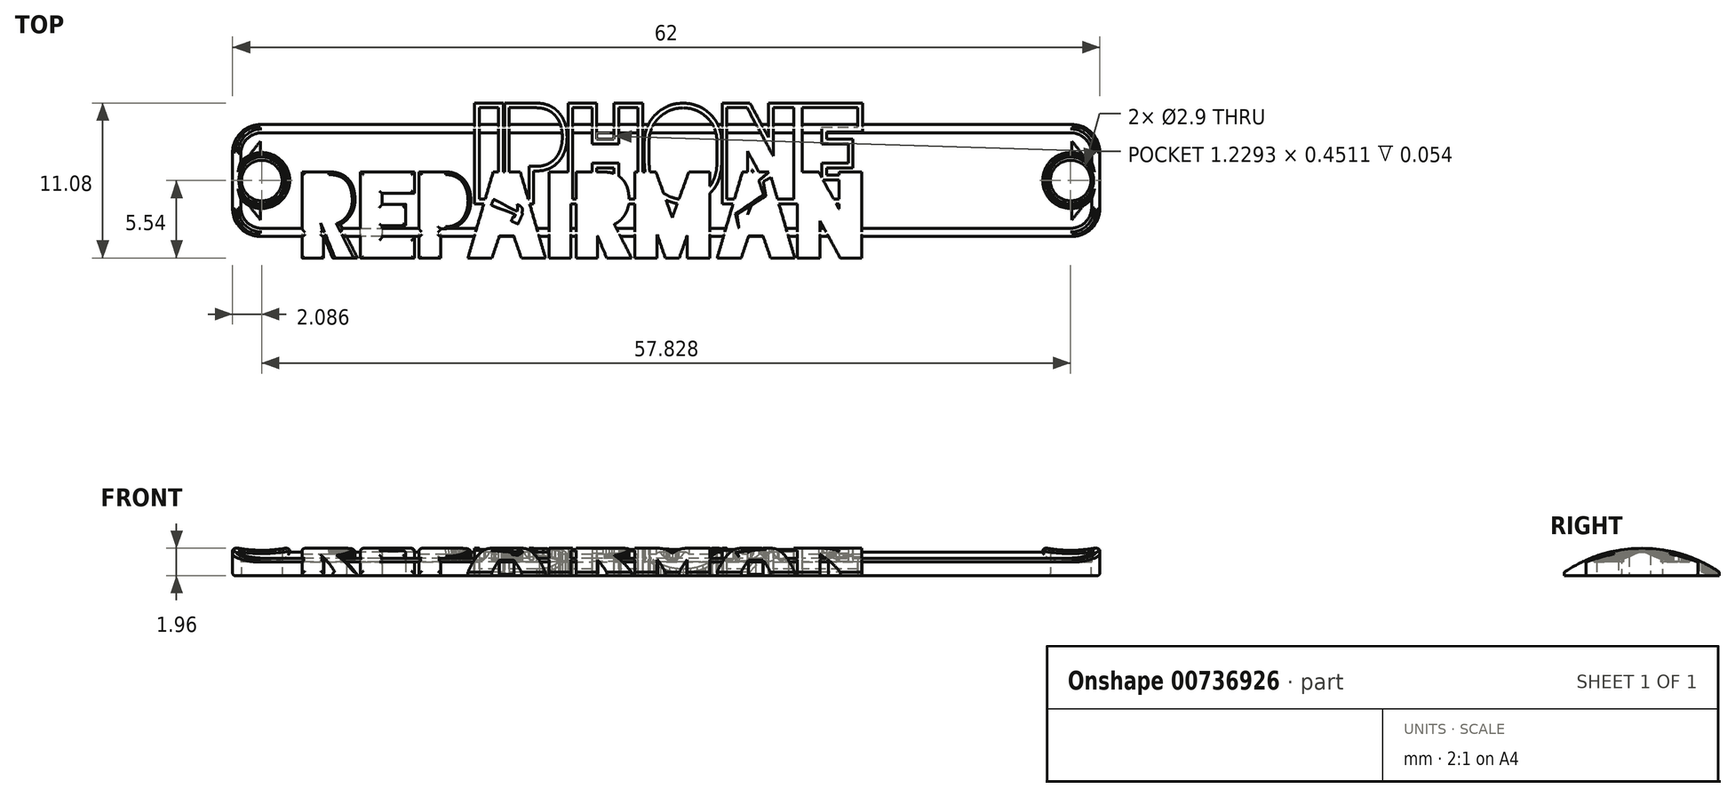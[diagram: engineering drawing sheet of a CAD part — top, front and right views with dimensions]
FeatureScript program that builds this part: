
annotation { "Feature Type Name" : "Feature", "Feature Type Description" : "" }
export const myFeature = defineFeature(function(context is Context, id is Id, definition is map)
    precondition{}
    {
        {
            var Q0;
            Q0=qCreatedBy(makeId("Top.planeOp"),FACE);
            var sketch = newSketch(context, id + "F0", { "sketchPlane" : qUnion([Q0])});
            skLineSegment(sketch, "E0", {"start": v(19.57, 7.6) * mm, "end": v(19.84, 6.63) * mm});
            skLineSegment(sketch, "E1", {"start": v(19.84, 6.63) * mm, "end": v(19.94, 5.63) * mm});
            skLineSegment(sketch, "E2", {"start": v(19.94, 5.63) * mm, "end": v(19.94, 5.62) * mm});
            skLineSegment(sketch, "E3", {"start": v(19.94, 5.62) * mm, "end": v(19.94, 2.5) * mm});
            skLineSegment(sketch, "E4", {"start": v(19.94, 2.5) * mm, "end": v(19.86, 1.44) * mm});
            skLineSegment(sketch, "E5", {"start": v(19.86, 1.44) * mm, "end": v(19.6, 0.37) * mm});
            skLineSegment(sketch, "E6", {"start": v(19.6, 0.37) * mm, "end": v(19.51, 0.1) * mm});
            skLineSegment(sketch, "E7", {"start": v(19.51, 0.1) * mm, "end": v(19.41, -0.17) * mm});
            skLineSegment(sketch, "E8", {"start": v(19.41, -0.17) * mm, "end": v(19.3, -0.42) * mm});
            skLineSegment(sketch, "E9", {"start": v(19.3, -0.42) * mm, "end": v(19.16, -0.67) * mm});
            skLineSegment(sketch, "E10", {"start": v(19.16, -0.67) * mm, "end": v(19.02, -0.9) * mm});
            skLineSegment(sketch, "E11", {"start": v(19.02, -0.9) * mm, "end": v(18.86, -1.14) * mm});
            skLineSegment(sketch, "E12", {"start": v(18.86, -1.14) * mm, "end": v(18.68, -1.36) * mm});
            skLineSegment(sketch, "E13", {"start": v(18.68, -1.36) * mm, "end": v(18.5, -1.57) * mm});
            skLineSegment(sketch, "E14", {"start": v(18.5, -1.57) * mm, "end": v(18.5, -1.57) * mm});
            skLineSegment(sketch, "E15", {"start": v(18.5, -1.57) * mm, "end": v(18.25, -1.82) * mm});
            skLineSegment(sketch, "E16", {"start": v(18.25, -1.82) * mm, "end": v(18.25, -11.08) * mm});
            skLineSegment(sketch, "E17", {"start": v(18.25, -11.08) * mm, "end": v(15, -11.08) * mm});
            skLineSegment(sketch, "E18", {"start": v(15, -11.08) * mm, "end": v(15, -7.86) * mm});
            skLineSegment(sketch, "E19", {"start": v(15, -7.86) * mm, "end": v(13.87, -11.08) * mm});
            skLineSegment(sketch, "E20", {"start": v(13.87, -11.08) * mm, "end": v(11.88, -11.08) * mm});
            skLineSegment(sketch, "E21", {"start": v(11.88, -11.08) * mm, "end": v(10.7, -7.7) * mm});
            skLineSegment(sketch, "E22", {"start": v(10.7, -7.7) * mm, "end": v(10.7, -11.08) * mm});
            skLineSegment(sketch, "E23", {"start": v(10.7, -11.08) * mm, "end": v(7.48, -11.08) * mm});
            skLineSegment(sketch, "E24", {"start": v(7.48, -11.08) * mm, "end": v(7.48, -3.35) * mm});
            skLineSegment(sketch, "E25", {"start": v(7.48, -3.35) * mm, "end": v(6.65, -3.35) * mm});
            skLineSegment(sketch, "E26", {"start": v(6.65, -3.35) * mm, "end": v(6.46, -4.12) * mm});
            skLineSegment(sketch, "E27", {"start": v(6.46, -4.12) * mm, "end": v(6.35, -4.4) * mm});
            skLineSegment(sketch, "E28", {"start": v(6.35, -4.4) * mm, "end": v(6.21, -4.68) * mm});
            skLineSegment(sketch, "E29", {"start": v(6.21, -4.68) * mm, "end": v(6.07, -4.92) * mm});
            skLineSegment(sketch, "E30", {"start": v(6.07, -4.92) * mm, "end": v(5.91, -5.15) * mm});
            skLineSegment(sketch, "E31", {"start": v(5.91, -5.15) * mm, "end": v(5.75, -5.36) * mm});
            skLineSegment(sketch, "E32", {"start": v(5.75, -5.36) * mm, "end": v(5.58, -5.54) * mm});
            skLineSegment(sketch, "E33", {"start": v(5.58, -5.54) * mm, "end": v(5.4, -5.71) * mm});
            skLineSegment(sketch, "E34", {"start": v(5.4, -5.71) * mm, "end": v(5.22, -5.86) * mm});
            skLineSegment(sketch, "E35", {"start": v(5.22, -5.86) * mm, "end": v(5.05, -6) * mm});
            skLineSegment(sketch, "E36", {"start": v(5.05, -6) * mm, "end": v(4.88, -6.1) * mm});
            skLineSegment(sketch, "E37", {"start": v(4.88, -6.1) * mm, "end": v(4.73, -6.19) * mm});
            skLineSegment(sketch, "E38", {"start": v(4.73, -6.19) * mm, "end": v(4.58, -6.25) * mm});
            skLineSegment(sketch, "E39", {"start": v(4.58, -6.25) * mm, "end": v(5.82, -8.67) * mm});
            skLineSegment(sketch, "E40", {"start": v(5.82, -8.67) * mm, "end": v(7.04, -11.08) * mm});
            skLineSegment(sketch, "E41", {"start": v(7.04, -11.08) * mm, "end": v(3.5, -11.08) * mm});
            skLineSegment(sketch, "E42", {"start": v(3.5, -11.08) * mm, "end": v(2.18, -7.94) * mm});
            skLineSegment(sketch, "E43", {"start": v(2.18, -7.94) * mm, "end": v(2.18, -11.08) * mm});
            skLineSegment(sketch, "E44", {"start": v(2.18, -11.08) * mm, "end": v(-0.9, -11.08) * mm});
            skLineSegment(sketch, "E45", {"start": v(-0.9, -11.08) * mm, "end": v(-0.9, -3.35) * mm});
            skLineSegment(sketch, "E46", {"start": v(-0.9, -3.35) * mm, "end": v(-1.66, -3.35) * mm});
            skLineSegment(sketch, "E47", {"start": v(-1.66, -3.35) * mm, "end": v(-1.66, -11.08) * mm});
            skLineSegment(sketch, "E48", {"start": v(-1.66, -11.08) * mm, "end": v(-4.74, -11.08) * mm});
            skLineSegment(sketch, "E49", {"start": v(-4.74, -11.08) * mm, "end": v(-4.74, 1.23) * mm});
            skLineSegment(sketch, "E50", {"start": v(-4.74, 1.23) * mm, "end": v(-2.03, 1.23) * mm});
            skLineSegment(sketch, "E51", {"start": v(-2.03, 1.23) * mm, "end": v(-2.03, 11.08) * mm});
            skLineSegment(sketch, "E52", {"start": v(-2.03, 11.08) * mm, "end": v(2.08, 11.08) * mm});
            skLineSegment(sketch, "E53", {"start": v(2.08, 11.08) * mm, "end": v(2.08, 5.93) * mm});
            skLineSegment(sketch, "E54", {"start": v(2.08, 5.93) * mm, "end": v(4.54, 5.93) * mm});
            skLineSegment(sketch, "E55", {"start": v(4.54, 5.93) * mm, "end": v(4.54, 11.08) * mm});
            skLineSegment(sketch, "E56", {"start": v(4.54, 11.08) * mm, "end": v(4.88, 11.08) * mm});
            skLineSegment(sketch, "E57", {"start": v(4.88, 11.08) * mm, "end": v(8.65, 11.08) * mm});
            skLineSegment(sketch, "E58", {"start": v(8.65, 11.08) * mm, "end": v(8.65, 1.23) * mm});
            skLineSegment(sketch, "E59", {"start": v(8.65, 1.23) * mm, "end": v(8.98, 1.23) * mm});
            skLineSegment(sketch, "E60", {"start": v(8.98, 1.23) * mm, "end": v(8.96, 1.38) * mm});
            skLineSegment(sketch, "E61", {"start": v(8.96, 1.38) * mm, "end": v(8.87, 2.5) * mm});
            skLineSegment(sketch, "E62", {"start": v(8.87, 2.5) * mm, "end": v(8.87, 2.5) * mm});
            skLineSegment(sketch, "E63", {"start": v(8.87, 2.5) * mm, "end": v(8.87, 5.62) * mm});
            skLineSegment(sketch, "E64", {"start": v(8.87, 5.62) * mm, "end": v(8.96, 6.6) * mm});
            skLineSegment(sketch, "E65", {"start": v(8.96, 6.6) * mm, "end": v(9.24, 7.58) * mm});
            skLineSegment(sketch, "E66", {"start": v(9.24, 7.58) * mm, "end": v(9.7, 8.5) * mm});
            skLineSegment(sketch, "E67", {"start": v(9.7, 8.5) * mm, "end": v(10.32, 9.3) * mm});
            skLineSegment(sketch, "E68", {"start": v(10.32, 9.3) * mm, "end": v(10.32, 9.3) * mm});
            skLineSegment(sketch, "E69", {"start": v(10.32, 9.3) * mm, "end": v(11.2, 10.06) * mm});
            skLineSegment(sketch, "E70", {"start": v(11.2, 10.06) * mm, "end": v(12.2, 10.62) * mm});
            skLineSegment(sketch, "E71", {"start": v(12.2, 10.62) * mm, "end": v(12.2, 10.62) * mm});
            skLineSegment(sketch, "E72", {"start": v(12.2, 10.62) * mm, "end": v(12.46, 10.73) * mm});
            skLineSegment(sketch, "E73", {"start": v(12.46, 10.73) * mm, "end": v(12.72, 10.82) * mm});
            skLineSegment(sketch, "E74", {"start": v(12.72, 10.82) * mm, "end": v(13, 10.9) * mm});
            skLineSegment(sketch, "E75", {"start": v(13, 10.9) * mm, "end": v(13.27, 10.97) * mm});
            skLineSegment(sketch, "E76", {"start": v(13.27, 10.97) * mm, "end": v(14.42, 11.08) * mm});
            skLineSegment(sketch, "E77", {"start": v(14.42, 11.08) * mm, "end": v(15.56, 10.96) * mm});
            skLineSegment(sketch, "E78", {"start": v(15.56, 10.96) * mm, "end": v(16.64, 10.62) * mm});
            skLineSegment(sketch, "E79", {"start": v(16.64, 10.62) * mm, "end": v(16.9, 10.5) * mm});
            skLineSegment(sketch, "E80", {"start": v(16.9, 10.5) * mm, "end": v(17.15, 10.37) * mm});
            skLineSegment(sketch, "E81", {"start": v(17.15, 10.37) * mm, "end": v(17.4, 10.22) * mm});
            skLineSegment(sketch, "E82", {"start": v(17.4, 10.22) * mm, "end": v(17.63, 10.06) * mm});
            skLineSegment(sketch, "E83", {"start": v(17.63, 10.06) * mm, "end": v(18.5, 9.3) * mm});
            skLineSegment(sketch, "E84", {"start": v(18.5, 9.3) * mm, "end": v(19.12, 8.51) * mm});
            skLineSegment(sketch, "E85", {"start": v(19.12, 8.51) * mm, "end": v(19.57, 7.6) * mm});
            skLineSegment(sketch, "E86", {"start": v(7.48, -2.67) * mm, "end": v(7.48, 1.23) * mm});
            skLineSegment(sketch, "E87", {"start": v(7.48, 1.23) * mm, "end": v(7.97, 1.23) * mm});
            skLineSegment(sketch, "E88", {"start": v(7.97, 1.23) * mm, "end": v(7.97, 10.4) * mm});
            skLineSegment(sketch, "E89", {"start": v(7.97, 10.4) * mm, "end": v(5.22, 10.4) * mm});
            skLineSegment(sketch, "E90", {"start": v(5.22, 10.4) * mm, "end": v(5.22, 5.25) * mm});
            skLineSegment(sketch, "E91", {"start": v(5.22, 5.25) * mm, "end": v(1.4, 5.25) * mm});
            skLineSegment(sketch, "E92", {"start": v(1.4, 5.25) * mm, "end": v(1.4, 10.4) * mm});
            skLineSegment(sketch, "E93", {"start": v(1.4, 10.4) * mm, "end": v(-1.35, 10.4) * mm});
            skLineSegment(sketch, "E94", {"start": v(-1.35, 10.4) * mm, "end": v(-1.35, -2.67) * mm});
            skLineSegment(sketch, "E95", {"start": v(-1.35, -2.67) * mm, "end": v(-0.9, -2.67) * mm});
            skLineSegment(sketch, "E96", {"start": v(-0.9, -2.67) * mm, "end": v(-0.9, 1.23) * mm});
            skLineSegment(sketch, "E97", {"start": v(-0.9, 1.23) * mm, "end": v(1.4, 1.23) * mm});
            skLineSegment(sketch, "E98", {"start": v(1.4, 1.23) * mm, "end": v(1.4, 2.48) * mm});
            skLineSegment(sketch, "E99", {"start": v(1.4, 2.48) * mm, "end": v(5.22, 2.48) * mm});
            skLineSegment(sketch, "E100", {"start": v(5.22, 2.48) * mm, "end": v(5.22, 0.64) * mm});
            skLineSegment(sketch, "E101", {"start": v(5.22, 0.64) * mm, "end": v(5.4, 0.5) * mm});
            skLineSegment(sketch, "E102", {"start": v(5.4, 0.5) * mm, "end": v(5.58, 0.35) * mm});
            skLineSegment(sketch, "E103", {"start": v(5.58, 0.35) * mm, "end": v(5.74, 0.2) * mm});
            skLineSegment(sketch, "E104", {"start": v(5.74, 0.2) * mm, "end": v(5.89, 0.02) * mm});
            skLineSegment(sketch, "E105", {"start": v(5.89, 0.02) * mm, "end": v(6.09, -0.26) * mm});
            skLineSegment(sketch, "E106", {"start": v(6.09, -0.26) * mm, "end": v(6.26, -0.57) * mm});
            skLineSegment(sketch, "E107", {"start": v(6.26, -0.57) * mm, "end": v(6.4, -0.9) * mm});
            skLineSegment(sketch, "E108", {"start": v(6.4, -0.9) * mm, "end": v(6.5, -1.26) * mm});
            skLineSegment(sketch, "E109", {"start": v(6.5, -1.26) * mm, "end": v(6.58, -1.6) * mm});
            skLineSegment(sketch, "E110", {"start": v(6.58, -1.6) * mm, "end": v(6.64, -1.95) * mm});
            skLineSegment(sketch, "E111", {"start": v(6.64, -1.95) * mm, "end": v(6.67, -2.3) * mm});
            skLineSegment(sketch, "E112", {"start": v(6.67, -2.3) * mm, "end": v(6.69, -2.67) * mm});
            skLineSegment(sketch, "E113", {"start": v(6.69, -2.67) * mm, "end": v(7.48, -2.67) * mm});
            skLineSegment(sketch, "E114", {"start": v(4.54, 0.99) * mm, "end": v(4.54, 1.8) * mm});
            skLineSegment(sketch, "E115", {"start": v(4.54, 1.8) * mm, "end": v(2.08, 1.8) * mm});
            skLineSegment(sketch, "E116", {"start": v(2.08, 1.8) * mm, "end": v(2.08, 1.23) * mm});
            skLineSegment(sketch, "E117", {"start": v(2.08, 1.23) * mm, "end": v(2.94, 1.23) * mm});
            skLineSegment(sketch, "E118", {"start": v(2.94, 1.23) * mm, "end": v(3.4, 1.21) * mm});
            skLineSegment(sketch, "E119", {"start": v(3.4, 1.21) * mm, "end": v(3.8, 1.17) * mm});
            skLineSegment(sketch, "E120", {"start": v(3.8, 1.17) * mm, "end": v(4.19, 1.1) * mm});
            skLineSegment(sketch, "E121", {"start": v(4.19, 1.1) * mm, "end": v(4.54, 0.99) * mm});
            skLineSegment(sketch, "E122", {"start": v(13.59, -3.3) * mm, "end": v(13.27, -3.25) * mm});
            skLineSegment(sketch, "E123", {"start": v(13.27, -3.25) * mm, "end": v(12.2, -2.9) * mm});
            skLineSegment(sketch, "E124", {"start": v(12.2, -2.9) * mm, "end": v(11.98, -2.8) * mm});
            skLineSegment(sketch, "E125", {"start": v(11.98, -2.8) * mm, "end": v(12.88, -5.3) * mm});
            skLineSegment(sketch, "E126", {"start": v(12.88, -5.3) * mm, "end": v(13.59, -3.3) * mm});
            skLineSegment(sketch, "E127", {"start": v(15.23, 1.23) * mm, "end": v(18.25, 1.23) * mm});
            skLineSegment(sketch, "E128", {"start": v(18.25, 1.23) * mm, "end": v(18.25, -0.82) * mm});
            skLineSegment(sketch, "E129", {"start": v(18.25, -0.82) * mm, "end": v(18.58, -0.33) * mm});
            skLineSegment(sketch, "E130", {"start": v(18.58, -0.33) * mm, "end": v(18.96, 0.56) * mm});
            skLineSegment(sketch, "E131", {"start": v(18.96, 0.56) * mm, "end": v(18.96, 0.57) * mm});
            skLineSegment(sketch, "E132", {"start": v(18.96, 0.57) * mm, "end": v(19.2, 1.54) * mm});
            skLineSegment(sketch, "E133", {"start": v(19.2, 1.54) * mm, "end": v(19.27, 2.5) * mm});
            skLineSegment(sketch, "E134", {"start": v(19.27, 2.5) * mm, "end": v(19.27, 5.62) * mm});
            skLineSegment(sketch, "E135", {"start": v(19.27, 5.62) * mm, "end": v(19.27, 5.62) * mm});
            skLineSegment(sketch, "E136", {"start": v(19.27, 5.62) * mm, "end": v(19.18, 6.51) * mm});
            skLineSegment(sketch, "E137", {"start": v(19.18, 6.51) * mm, "end": v(18.94, 7.36) * mm});
            skLineSegment(sketch, "E138", {"start": v(18.94, 7.36) * mm, "end": v(18.94, 7.37) * mm});
            skLineSegment(sketch, "E139", {"start": v(18.94, 7.37) * mm, "end": v(18.55, 8.15) * mm});
            skLineSegment(sketch, "E140", {"start": v(18.55, 8.15) * mm, "end": v(18.01, 8.84) * mm});
            skLineSegment(sketch, "E141", {"start": v(18.01, 8.84) * mm, "end": v(18, 8.84) * mm});
            skLineSegment(sketch, "E142", {"start": v(18, 8.84) * mm, "end": v(17.24, 9.51) * mm});
            skLineSegment(sketch, "E143", {"start": v(17.24, 9.51) * mm, "end": v(16.37, 10) * mm});
            skLineSegment(sketch, "E144", {"start": v(16.37, 10) * mm, "end": v(15.42, 10.3) * mm});
            skLineSegment(sketch, "E145", {"start": v(15.42, 10.3) * mm, "end": v(14.42, 10.4) * mm});
            skLineSegment(sketch, "E146", {"start": v(14.42, 10.4) * mm, "end": v(13.4, 10.3) * mm});
            skLineSegment(sketch, "E147", {"start": v(13.4, 10.3) * mm, "end": v(12.47, 10) * mm});
            skLineSegment(sketch, "E148", {"start": v(12.47, 10) * mm, "end": v(11.59, 9.5) * mm});
            skLineSegment(sketch, "E149", {"start": v(11.59, 9.5) * mm, "end": v(10.81, 8.84) * mm});
            skLineSegment(sketch, "E150", {"start": v(10.81, 8.84) * mm, "end": v(10.27, 8.14) * mm});
            skLineSegment(sketch, "E151", {"start": v(10.27, 8.14) * mm, "end": v(9.88, 7.34) * mm});
            skLineSegment(sketch, "E152", {"start": v(9.88, 7.34) * mm, "end": v(9.88, 7.34) * mm});
            skLineSegment(sketch, "E153", {"start": v(9.88, 7.34) * mm, "end": v(9.63, 6.47) * mm});
            skLineSegment(sketch, "E154", {"start": v(9.63, 6.47) * mm, "end": v(9.55, 5.62) * mm});
            skLineSegment(sketch, "E155", {"start": v(9.55, 5.62) * mm, "end": v(9.55, 2.5) * mm});
            skLineSegment(sketch, "E156", {"start": v(9.55, 2.5) * mm, "end": v(9.55, 2.5) * mm});
            skLineSegment(sketch, "E157", {"start": v(9.55, 2.5) * mm, "end": v(9.63, 1.48) * mm});
            skLineSegment(sketch, "E158", {"start": v(9.63, 1.48) * mm, "end": v(9.67, 1.23) * mm});
            skLineSegment(sketch, "E159", {"start": v(9.67, 1.23) * mm, "end": v(10.53, 1.23) * mm});
            skLineSegment(sketch, "E160", {"start": v(10.53, 1.23) * mm, "end": v(11.63, -1.82) * mm});
            skLineSegment(sketch, "E161", {"start": v(11.63, -1.82) * mm, "end": v(12.47, -2.29) * mm});
            skLineSegment(sketch, "E162", {"start": v(12.47, -2.29) * mm, "end": v(13.4, -2.59) * mm});
            skLineSegment(sketch, "E163", {"start": v(13.4, -2.59) * mm, "end": v(13.4, -2.59) * mm});
            skLineSegment(sketch, "E164", {"start": v(13.4, -2.59) * mm, "end": v(13.82, -2.65) * mm});
            skLineSegment(sketch, "E165", {"start": v(13.82, -2.65) * mm, "end": v(14.05, -2.03) * mm});
            skLineSegment(sketch, "E166", {"start": v(14.05, -2.03) * mm, "end": v(15.23, 1.23) * mm});
            skLineSegment(sketch, "E167", {"start": v(26.97, 11.08) * mm, "end": v(30.92, 11.08) * mm});
            skLineSegment(sketch, "E168", {"start": v(30.92, 11.08) * mm, "end": v(30.92, -3.35) * mm});
            skLineSegment(sketch, "E169", {"start": v(30.92, -3.35) * mm, "end": v(28.11, -3.35) * mm});
            skLineSegment(sketch, "E170", {"start": v(28.11, -3.35) * mm, "end": v(30.37, -11.08) * mm});
            skLineSegment(sketch, "E171", {"start": v(30.37, -11.08) * mm, "end": v(26.93, -11.08) * mm});
            skLineSegment(sketch, "E172", {"start": v(26.93, -11.08) * mm, "end": v(25.84, -7.94) * mm});
            skLineSegment(sketch, "E173", {"start": v(25.84, -7.94) * mm, "end": v(23.79, -7.94) * mm});
            skLineSegment(sketch, "E174", {"start": v(23.79, -7.94) * mm, "end": v(22.73, -11.08) * mm});
            skLineSegment(sketch, "E175", {"start": v(22.73, -11.08) * mm, "end": v(19.29, -11.08) * mm});
            skLineSegment(sketch, "E176", {"start": v(19.29, -11.08) * mm, "end": v(21.55, -3.35) * mm});
            skLineSegment(sketch, "E177", {"start": v(21.55, -3.35) * mm, "end": v(20, -3.35) * mm});
            skLineSegment(sketch, "E178", {"start": v(20, -3.35) * mm, "end": v(20, 11.08) * mm});
            skLineSegment(sketch, "E179", {"start": v(20, 11.08) * mm, "end": v(23.96, 11.08) * mm});
            skLineSegment(sketch, "E180", {"start": v(23.96, 11.08) * mm, "end": v(26.63, 6.17) * mm});
            skLineSegment(sketch, "E181", {"start": v(26.63, 6.17) * mm, "end": v(26.63, 11.08) * mm});
            skLineSegment(sketch, "E182", {"start": v(26.63, 11.08) * mm, "end": v(26.97, 11.08) * mm});
            skLineSegment(sketch, "E183", {"start": v(24.48, 1.23) * mm, "end": v(24.3, 1.57) * mm});
            skLineSegment(sketch, "E184", {"start": v(24.3, 1.57) * mm, "end": v(24.3, 1.23) * mm});
            skLineSegment(sketch, "E185", {"start": v(24.3, 1.23) * mm, "end": v(24.48, 1.23) * mm});
            skLineSegment(sketch, "E186", {"start": v(27, 0.44) * mm, "end": v(27.91, -2.67) * mm});
            skLineSegment(sketch, "E187", {"start": v(27.91, -2.67) * mm, "end": v(30.25, -2.67) * mm});
            skLineSegment(sketch, "E188", {"start": v(30.25, -2.67) * mm, "end": v(30.25, 10.4) * mm});
            skLineSegment(sketch, "E189", {"start": v(30.25, 10.4) * mm, "end": v(27.3, 10.4) * mm});
            skLineSegment(sketch, "E190", {"start": v(27.3, 10.4) * mm, "end": v(27.3, 3.5) * mm});
            skLineSegment(sketch, "E191", {"start": v(27.3, 3.5) * mm, "end": v(23.56, 10.4) * mm});
            skLineSegment(sketch, "E192", {"start": v(23.56, 10.4) * mm, "end": v(20.68, 10.4) * mm});
            skLineSegment(sketch, "E193", {"start": v(20.68, 10.4) * mm, "end": v(20.68, -2.67) * mm});
            skLineSegment(sketch, "E194", {"start": v(20.68, -2.67) * mm, "end": v(21.75, -2.67) * mm});
            skLineSegment(sketch, "E195", {"start": v(21.75, -2.67) * mm, "end": v(22.9, 1.23) * mm});
            skLineSegment(sketch, "E196", {"start": v(22.9, 1.23) * mm, "end": v(23.62, 1.23) * mm});
            skLineSegment(sketch, "E197", {"start": v(23.62, 1.23) * mm, "end": v(23.62, 4.22) * mm});
            skLineSegment(sketch, "E198", {"start": v(23.62, 4.22) * mm, "end": v(25.25, 1.23) * mm});
            skLineSegment(sketch, "E199", {"start": v(25.25, 1.23) * mm, "end": v(26.71, 1.23) * mm});
            skLineSegment(sketch, "E200", {"start": v(26.71, 1.23) * mm, "end": v(25.25, -0.02) * mm});
            skLineSegment(sketch, "E201", {"start": v(25.25, -0.02) * mm, "end": v(25.9, -2) * mm});
            skLineSegment(sketch, "E202", {"start": v(25.9, -2) * mm, "end": v(21.89, -4.75) * mm});
            skLineSegment(sketch, "E203", {"start": v(21.89, -4.75) * mm, "end": v(22.4, -6.86) * mm});
            skLineSegment(sketch, "E204", {"start": v(22.4, -6.86) * mm, "end": v(22.1, -4.84) * mm});
            skLineSegment(sketch, "E205", {"start": v(22.1, -4.84) * mm, "end": v(24.02, -3.63) * mm});
            skLineSegment(sketch, "E206", {"start": v(24.02, -3.63) * mm, "end": v(23.63, -4.9) * mm});
            skLineSegment(sketch, "E207", {"start": v(23.63, -4.9) * mm, "end": v(24.23, -3.5) * mm});
            skLineSegment(sketch, "E208", {"start": v(24.23, -3.5) * mm, "end": v(26.24, -2.23) * mm});
            skLineSegment(sketch, "E209", {"start": v(26.24, -2.23) * mm, "end": v(25.88, -0.14) * mm});
            skLineSegment(sketch, "E210", {"start": v(25.88, -0.14) * mm, "end": v(27, 0.44) * mm});
            skLineSegment(sketch, "E211", {"start": v(-33.37, -8.67) * mm, "end": v(-32.14, -11.08) * mm});
            skLineSegment(sketch, "E212", {"start": v(-32.14, -11.08) * mm, "end": v(-35.69, -11.08) * mm});
            skLineSegment(sketch, "E213", {"start": v(-35.69, -11.08) * mm, "end": v(-37, -7.94) * mm});
            skLineSegment(sketch, "E214", {"start": v(-37, -7.94) * mm, "end": v(-37, -11.08) * mm});
            skLineSegment(sketch, "E215", {"start": v(-37, -11.08) * mm, "end": v(-40.07, -11.08) * mm});
            skLineSegment(sketch, "E216", {"start": v(-40.07, -11.08) * mm, "end": v(-40.07, 1.23) * mm});
            skLineSegment(sketch, "E217", {"start": v(-40.07, 1.23) * mm, "end": v(-36.24, 1.23) * mm});
            skLineSegment(sketch, "E218", {"start": v(-36.24, 1.23) * mm, "end": v(-35.98, 1.22) * mm});
            skLineSegment(sketch, "E219", {"start": v(-35.98, 1.22) * mm, "end": v(-35.73, 1.2) * mm});
            skLineSegment(sketch, "E220", {"start": v(-35.73, 1.2) * mm, "end": v(-35.49, 1.18) * mm});
            skLineSegment(sketch, "E221", {"start": v(-35.49, 1.18) * mm, "end": v(-35.26, 1.15) * mm});
            skLineSegment(sketch, "E222", {"start": v(-35.26, 1.15) * mm, "end": v(-35.04, 1.1) * mm});
            skLineSegment(sketch, "E223", {"start": v(-35.04, 1.1) * mm, "end": v(-34.83, 1.05) * mm});
            skLineSegment(sketch, "E224", {"start": v(-34.83, 1.05) * mm, "end": v(-34.63, 0.98) * mm});
            skLineSegment(sketch, "E225", {"start": v(-34.63, 0.98) * mm, "end": v(-34.45, 0.9) * mm});
            skLineSegment(sketch, "E226", {"start": v(-34.45, 0.9) * mm, "end": v(-34.27, 0.82) * mm});
            skLineSegment(sketch, "E227", {"start": v(-34.27, 0.82) * mm, "end": v(-34.1, 0.73) * mm});
            skLineSegment(sketch, "E228", {"start": v(-34.1, 0.73) * mm, "end": v(-33.95, 0.63) * mm});
            skLineSegment(sketch, "E229", {"start": v(-33.95, 0.63) * mm, "end": v(-33.8, 0.52) * mm});
            skLineSegment(sketch, "E230", {"start": v(-33.8, 0.52) * mm, "end": v(-33.66, 0.4) * mm});
            skLineSegment(sketch, "E231", {"start": v(-33.66, 0.4) * mm, "end": v(-33.53, 0.28) * mm});
            skLineSegment(sketch, "E232", {"start": v(-33.53, 0.28) * mm, "end": v(-33.4, 0.16) * mm});
            skLineSegment(sketch, "E233", {"start": v(-33.4, 0.16) * mm, "end": v(-33.3, 0.02) * mm});
            skLineSegment(sketch, "E234", {"start": v(-33.3, 0.02) * mm, "end": v(-33.1, -0.26) * mm});
            skLineSegment(sketch, "E235", {"start": v(-33.1, -0.26) * mm, "end": v(-32.92, -0.57) * mm});
            skLineSegment(sketch, "E236", {"start": v(-32.92, -0.57) * mm, "end": v(-32.79, -0.9) * mm});
            skLineSegment(sketch, "E237", {"start": v(-32.79, -0.9) * mm, "end": v(-32.68, -1.26) * mm});
            skLineSegment(sketch, "E238", {"start": v(-32.68, -1.26) * mm, "end": v(-32.6, -1.63) * mm});
            skLineSegment(sketch, "E239", {"start": v(-32.6, -1.63) * mm, "end": v(-32.54, -2) * mm});
            skLineSegment(sketch, "E240", {"start": v(-32.54, -2) * mm, "end": v(-32.5, -2.4) * mm});
            skLineSegment(sketch, "E241", {"start": v(-32.5, -2.4) * mm, "end": v(-32.5, -2.8) * mm});
            skLineSegment(sketch, "E242", {"start": v(-32.5, -2.8) * mm, "end": v(-32.51, -3.15) * mm});
            skLineSegment(sketch, "E243", {"start": v(-32.51, -3.15) * mm, "end": v(-32.55, -3.49) * mm});
            skLineSegment(sketch, "E244", {"start": v(-32.55, -3.49) * mm, "end": v(-32.62, -3.81) * mm});
            skLineSegment(sketch, "E245", {"start": v(-32.62, -3.81) * mm, "end": v(-32.72, -4.12) * mm});
            skLineSegment(sketch, "E246", {"start": v(-32.72, -4.12) * mm, "end": v(-32.83, -4.4) * mm});
            skLineSegment(sketch, "E247", {"start": v(-32.83, -4.4) * mm, "end": v(-32.97, -4.68) * mm});
            skLineSegment(sketch, "E248", {"start": v(-32.97, -4.68) * mm, "end": v(-33.12, -4.92) * mm});
            skLineSegment(sketch, "E249", {"start": v(-33.12, -4.92) * mm, "end": v(-33.27, -5.15) * mm});
            skLineSegment(sketch, "E250", {"start": v(-33.27, -5.15) * mm, "end": v(-33.44, -5.36) * mm});
            skLineSegment(sketch, "E251", {"start": v(-33.44, -5.36) * mm, "end": v(-33.6, -5.54) * mm});
            skLineSegment(sketch, "E252", {"start": v(-33.6, -5.54) * mm, "end": v(-33.78, -5.71) * mm});
            skLineSegment(sketch, "E253", {"start": v(-33.78, -5.71) * mm, "end": v(-33.96, -5.86) * mm});
            skLineSegment(sketch, "E254", {"start": v(-33.96, -5.86) * mm, "end": v(-34.13, -6) * mm});
            skLineSegment(sketch, "E255", {"start": v(-34.13, -6) * mm, "end": v(-34.3, -6.1) * mm});
            skLineSegment(sketch, "E256", {"start": v(-34.3, -6.1) * mm, "end": v(-34.46, -6.19) * mm});
            skLineSegment(sketch, "E257", {"start": v(-34.46, -6.19) * mm, "end": v(-34.61, -6.25) * mm});
            skLineSegment(sketch, "E258", {"start": v(-34.61, -6.25) * mm, "end": v(-33.37, -8.67) * mm});
            skLineSegment(sketch, "E259", {"start": v(-31.71, 1.23) * mm, "end": v(-24.01, 1.23) * mm});
            skLineSegment(sketch, "E260", {"start": v(-24.01, 1.23) * mm, "end": v(-24.01, -1.85) * mm});
            skLineSegment(sketch, "E261", {"start": v(-24.01, -1.85) * mm, "end": v(-28.63, -1.85) * mm});
            skLineSegment(sketch, "E262", {"start": v(-28.63, -1.85) * mm, "end": v(-28.63, -3.38) * mm});
            skLineSegment(sketch, "E263", {"start": v(-28.63, -3.38) * mm, "end": v(-25.24, -3.38) * mm});
            skLineSegment(sketch, "E264", {"start": v(-25.24, -3.38) * mm, "end": v(-25.24, -6.46) * mm});
            skLineSegment(sketch, "E265", {"start": v(-25.24, -6.46) * mm, "end": v(-28.63, -6.46) * mm});
            skLineSegment(sketch, "E266", {"start": v(-28.63, -6.46) * mm, "end": v(-28.63, -8) * mm});
            skLineSegment(sketch, "E267", {"start": v(-28.63, -8) * mm, "end": v(-24.01, -8) * mm});
            skLineSegment(sketch, "E268", {"start": v(-24.01, -8) * mm, "end": v(-24.01, -11.08) * mm});
            skLineSegment(sketch, "E269", {"start": v(-24.01, -11.08) * mm, "end": v(-31.71, -11.08) * mm});
            skLineSegment(sketch, "E270", {"start": v(-31.71, -11.08) * mm, "end": v(-31.71, 1.23) * mm});
            skLineSegment(sketch, "E271", {"start": v(-16.2, -4.47) * mm, "end": v(-16.34, -4.83) * mm});
            skLineSegment(sketch, "E272", {"start": v(-16.34, -4.83) * mm, "end": v(-16.5, -5.16) * mm});
            skLineSegment(sketch, "E273", {"start": v(-16.5, -5.16) * mm, "end": v(-16.7, -5.47) * mm});
            skLineSegment(sketch, "E274", {"start": v(-16.7, -5.47) * mm, "end": v(-16.91, -5.75) * mm});
            skLineSegment(sketch, "E275", {"start": v(-16.91, -5.75) * mm, "end": v(-17.16, -6) * mm});
            skLineSegment(sketch, "E276", {"start": v(-17.16, -6) * mm, "end": v(-17.43, -6.23) * mm});
            skLineSegment(sketch, "E277", {"start": v(-17.43, -6.23) * mm, "end": v(-17.73, -6.42) * mm});
            skLineSegment(sketch, "E278", {"start": v(-17.73, -6.42) * mm, "end": v(-18.05, -6.58) * mm});
            skLineSegment(sketch, "E279", {"start": v(-18.05, -6.58) * mm, "end": v(-18.22, -6.65) * mm});
            skLineSegment(sketch, "E280", {"start": v(-18.22, -6.65) * mm, "end": v(-18.39, -6.71) * mm});
            skLineSegment(sketch, "E281", {"start": v(-18.39, -6.71) * mm, "end": v(-18.56, -6.76) * mm});
            skLineSegment(sketch, "E282", {"start": v(-18.56, -6.76) * mm, "end": v(-18.75, -6.8) * mm});
            skLineSegment(sketch, "E283", {"start": v(-18.75, -6.8) * mm, "end": v(-19.13, -6.86) * mm});
            skLineSegment(sketch, "E284", {"start": v(-19.13, -6.86) * mm, "end": v(-19.52, -6.88) * mm});
            skLineSegment(sketch, "E285", {"start": v(-19.52, -6.88) * mm, "end": v(-20.21, -6.88) * mm});
            skLineSegment(sketch, "E286", {"start": v(-20.21, -6.88) * mm, "end": v(-20.21, -11.08) * mm});
            skLineSegment(sketch, "E287", {"start": v(-20.21, -11.08) * mm, "end": v(-23.34, -11.08) * mm});
            skLineSegment(sketch, "E288", {"start": v(-23.34, -11.08) * mm, "end": v(-23.34, 1.23) * mm});
            skLineSegment(sketch, "E289", {"start": v(-23.34, 1.23) * mm, "end": v(-19.52, 1.23) * mm});
            skLineSegment(sketch, "E290", {"start": v(-19.52, 1.23) * mm, "end": v(-19.11, 1.21) * mm});
            skLineSegment(sketch, "E291", {"start": v(-19.11, 1.21) * mm, "end": v(-18.74, 1.16) * mm});
            skLineSegment(sketch, "E292", {"start": v(-18.74, 1.16) * mm, "end": v(-18.55, 1.12) * mm});
            skLineSegment(sketch, "E293", {"start": v(-18.55, 1.12) * mm, "end": v(-18.38, 1.07) * mm});
            skLineSegment(sketch, "E294", {"start": v(-18.38, 1.07) * mm, "end": v(-18.2, 1) * mm});
            skLineSegment(sketch, "E295", {"start": v(-18.2, 1) * mm, "end": v(-18.04, 0.94) * mm});
            skLineSegment(sketch, "E296", {"start": v(-18.04, 0.94) * mm, "end": v(-17.72, 0.78) * mm});
            skLineSegment(sketch, "E297", {"start": v(-17.72, 0.78) * mm, "end": v(-17.43, 0.6) * mm});
            skLineSegment(sketch, "E298", {"start": v(-17.43, 0.6) * mm, "end": v(-17.16, 0.37) * mm});
            skLineSegment(sketch, "E299", {"start": v(-17.16, 0.37) * mm, "end": v(-16.91, 0.13) * mm});
            skLineSegment(sketch, "E300", {"start": v(-16.91, 0.13) * mm, "end": v(-16.7, -0.15) * mm});
            skLineSegment(sketch, "E301", {"start": v(-16.7, -0.15) * mm, "end": v(-16.5, -0.46) * mm});
            skLineSegment(sketch, "E302", {"start": v(-16.5, -0.46) * mm, "end": v(-16.34, -0.79) * mm});
            skLineSegment(sketch, "E303", {"start": v(-16.34, -0.79) * mm, "end": v(-16.2, -1.15) * mm});
            skLineSegment(sketch, "E304", {"start": v(-16.2, -1.15) * mm, "end": v(-16.08, -1.53) * mm});
            skLineSegment(sketch, "E305", {"start": v(-16.08, -1.53) * mm, "end": v(-16, -1.94) * mm});
            skLineSegment(sketch, "E306", {"start": v(-16, -1.94) * mm, "end": v(-15.95, -2.37) * mm});
            skLineSegment(sketch, "E307", {"start": v(-15.95, -2.37) * mm, "end": v(-15.93, -2.82) * mm});
            skLineSegment(sketch, "E308", {"start": v(-15.93, -2.82) * mm, "end": v(-15.95, -3.26) * mm});
            skLineSegment(sketch, "E309", {"start": v(-15.95, -3.26) * mm, "end": v(-16, -3.68) * mm});
            skLineSegment(sketch, "E310", {"start": v(-16, -3.68) * mm, "end": v(-16.08, -4.08) * mm});
            skLineSegment(sketch, "E311", {"start": v(-16.08, -4.08) * mm, "end": v(-16.2, -4.47) * mm});
            skLineSegment(sketch, "E312", {"start": v(-8.87, 1.23) * mm, "end": v(-7.73, -2.67) * mm});
            skLineSegment(sketch, "E313", {"start": v(-7.73, -2.67) * mm, "end": v(-7.62, -2.67) * mm});
            skLineSegment(sketch, "E314", {"start": v(-7.62, -2.67) * mm, "end": v(-7.62, 2.02) * mm});
            skLineSegment(sketch, "E315", {"start": v(-7.62, 2.02) * mm, "end": v(-6.51, 2.02) * mm});
            skLineSegment(sketch, "E316", {"start": v(-6.51, 2.02) * mm, "end": v(-5.7, 2.1) * mm});
            skLineSegment(sketch, "E317", {"start": v(-5.7, 2.1) * mm, "end": v(-4.99, 2.32) * mm});
            skLineSegment(sketch, "E318", {"start": v(-4.99, 2.32) * mm, "end": v(-4.37, 2.69) * mm});
            skLineSegment(sketch, "E319", {"start": v(-4.37, 2.69) * mm, "end": v(-3.85, 3.16) * mm});
            skLineSegment(sketch, "E320", {"start": v(-3.85, 3.16) * mm, "end": v(-3.85, 3.16) * mm});
            skLineSegment(sketch, "E321", {"start": v(-3.85, 3.16) * mm, "end": v(-3.43, 3.77) * mm});
            skLineSegment(sketch, "E322", {"start": v(-3.43, 3.77) * mm, "end": v(-3.11, 4.48) * mm});
            skLineSegment(sketch, "E323", {"start": v(-3.11, 4.48) * mm, "end": v(-3.11, 4.48) * mm});
            skLineSegment(sketch, "E324", {"start": v(-3.11, 4.48) * mm, "end": v(-2.9, 5.3) * mm});
            skLineSegment(sketch, "E325", {"start": v(-2.9, 5.3) * mm, "end": v(-2.84, 6.2) * mm});
            skLineSegment(sketch, "E326", {"start": v(-2.84, 6.2) * mm, "end": v(-2.91, 7.15) * mm});
            skLineSegment(sketch, "E327", {"start": v(-2.91, 7.15) * mm, "end": v(-3.11, 7.98) * mm});
            skLineSegment(sketch, "E328", {"start": v(-3.11, 7.98) * mm, "end": v(-3.11, 7.98) * mm});
            skLineSegment(sketch, "E329", {"start": v(-3.11, 7.98) * mm, "end": v(-3.42, 8.68) * mm});
            skLineSegment(sketch, "E330", {"start": v(-3.42, 8.68) * mm, "end": v(-3.85, 9.28) * mm});
            skLineSegment(sketch, "E331", {"start": v(-3.85, 9.28) * mm, "end": v(-3.85, 9.28) * mm});
            skLineSegment(sketch, "E332", {"start": v(-3.85, 9.28) * mm, "end": v(-4.36, 9.76) * mm});
            skLineSegment(sketch, "E333", {"start": v(-4.36, 9.76) * mm, "end": v(-4.98, 10.1) * mm});
            skLineSegment(sketch, "E334", {"start": v(-4.98, 10.1) * mm, "end": v(-5.69, 10.33) * mm});
            skLineSegment(sketch, "E335", {"start": v(-5.69, 10.33) * mm, "end": v(-6.5, 10.4) * mm});
            skLineSegment(sketch, "E336", {"start": v(-6.5, 10.4) * mm, "end": v(-10.44, 10.4) * mm});
            skLineSegment(sketch, "E337", {"start": v(-10.44, 10.4) * mm, "end": v(-10.44, 1.23) * mm});
            skLineSegment(sketch, "E338", {"start": v(-10.44, 1.23) * mm, "end": v(-8.87, 1.23) * mm});
            skLineSegment(sketch, "E339", {"start": v(-9.19, -6.22) * mm, "end": v(-8.53, -4.76) * mm});
            skLineSegment(sketch, "E340", {"start": v(-8.53, -4.76) * mm, "end": v(-8.61, -4.65) * mm});
            skLineSegment(sketch, "E341", {"start": v(-8.61, -4.65) * mm, "end": v(-8.65, -4.57) * mm});
            skLineSegment(sketch, "E342", {"start": v(-8.65, -4.57) * mm, "end": v(-8.64, -4.5) * mm});
            skLineSegment(sketch, "E343", {"start": v(-8.64, -4.5) * mm, "end": v(-8.6, -4.44) * mm});
            skLineSegment(sketch, "E344", {"start": v(-8.6, -4.44) * mm, "end": v(-8.57, -4.36) * mm});
            skLineSegment(sketch, "E345", {"start": v(-8.57, -4.36) * mm, "end": v(-8.54, -4.27) * mm});
            skLineSegment(sketch, "E346", {"start": v(-8.54, -4.27) * mm, "end": v(-8.54, -4.15) * mm});
            skLineSegment(sketch, "E347", {"start": v(-8.54, -4.15) * mm, "end": v(-8.58, -3.98) * mm});
            skLineSegment(sketch, "E348", {"start": v(-8.58, -3.98) * mm, "end": v(-8.62, -3.9) * mm});
            skLineSegment(sketch, "E349", {"start": v(-8.62, -3.9) * mm, "end": v(-8.67, -3.83) * mm});
            skLineSegment(sketch, "E350", {"start": v(-8.67, -3.83) * mm, "end": v(-8.72, -3.77) * mm});
            skLineSegment(sketch, "E351", {"start": v(-8.72, -3.77) * mm, "end": v(-8.78, -3.71) * mm});
            skLineSegment(sketch, "E352", {"start": v(-8.78, -3.71) * mm, "end": v(-8.93, -3.61) * mm});
            skLineSegment(sketch, "E353", {"start": v(-8.93, -3.61) * mm, "end": v(-9.12, -3.52) * mm});
            skLineSegment(sketch, "E354", {"start": v(-9.12, -3.52) * mm, "end": v(-9.26, -3.46) * mm});
            skLineSegment(sketch, "E355", {"start": v(-9.26, -3.46) * mm, "end": v(-9.28, -3.45) * mm});
            skLineSegment(sketch, "E356", {"start": v(-9.28, -3.45) * mm, "end": v(-9.3, -3.44) * mm});
            skLineSegment(sketch, "E357", {"start": v(-9.3, -3.44) * mm, "end": v(-9.26, -3.67) * mm});
            skLineSegment(sketch, "E358", {"start": v(-9.26, -3.67) * mm, "end": v(-9.23, -3.88) * mm});
            skLineSegment(sketch, "E359", {"start": v(-9.23, -3.88) * mm, "end": v(-9.23, -4) * mm});
            skLineSegment(sketch, "E360", {"start": v(-9.23, -4) * mm, "end": v(-9.25, -4.12) * mm});
            skLineSegment(sketch, "E361", {"start": v(-9.25, -4.12) * mm, "end": v(-9.28, -4.25) * mm});
            skLineSegment(sketch, "E362", {"start": v(-9.28, -4.25) * mm, "end": v(-9.34, -4.4) * mm});
            skLineSegment(sketch, "E363", {"start": v(-9.34, -4.4) * mm, "end": v(-9.98, -4.1) * mm});
            skLineSegment(sketch, "E364", {"start": v(-9.98, -4.1) * mm, "end": v(-10.44, -3.87) * mm});
            skLineSegment(sketch, "E365", {"start": v(-10.44, -3.87) * mm, "end": v(-10.78, -3.69) * mm});
            skLineSegment(sketch, "E366", {"start": v(-10.78, -3.69) * mm, "end": v(-11.05, -3.53) * mm});
            skLineSegment(sketch, "E367", {"start": v(-11.05, -3.53) * mm, "end": v(-11.31, -3.37) * mm});
            skLineSegment(sketch, "E368", {"start": v(-11.31, -3.37) * mm, "end": v(-11.63, -3.2) * mm});
            skLineSegment(sketch, "E369", {"start": v(-11.63, -3.2) * mm, "end": v(-12.06, -2.98) * mm});
            skLineSegment(sketch, "E370", {"start": v(-12.06, -2.98) * mm, "end": v(-12.67, -2.7) * mm});
            skLineSegment(sketch, "E371", {"start": v(-12.67, -2.7) * mm, "end": v(-13.03, -3.51) * mm});
            skLineSegment(sketch, "E372", {"start": v(-13.03, -3.51) * mm, "end": v(-12.42, -3.78) * mm});
            skLineSegment(sketch, "E373", {"start": v(-12.42, -3.78) * mm, "end": v(-11.97, -3.96) * mm});
            skLineSegment(sketch, "E374", {"start": v(-11.97, -3.96) * mm, "end": v(-11.63, -4.08) * mm});
            skLineSegment(sketch, "E375", {"start": v(-11.63, -4.08) * mm, "end": v(-11.34, -4.18) * mm});
            skLineSegment(sketch, "E376", {"start": v(-11.34, -4.18) * mm, "end": v(-11.04, -4.28) * mm});
            skLineSegment(sketch, "E377", {"start": v(-11.04, -4.28) * mm, "end": v(-10.69, -4.4) * mm});
            skLineSegment(sketch, "E378", {"start": v(-10.69, -4.4) * mm, "end": v(-10.2, -4.6) * mm});
            skLineSegment(sketch, "E379", {"start": v(-10.2, -4.6) * mm, "end": v(-9.56, -4.88) * mm});
            skLineSegment(sketch, "E380", {"start": v(-9.56, -4.88) * mm, "end": v(-9.67, -5.13) * mm});
            skLineSegment(sketch, "E381", {"start": v(-9.67, -5.13) * mm, "end": v(-9.7, -5.2) * mm});
            skLineSegment(sketch, "E382", {"start": v(-9.7, -5.2) * mm, "end": v(-9.74, -5.17) * mm});
            skLineSegment(sketch, "E383", {"start": v(-9.74, -5.17) * mm, "end": v(-9.87, -5.14) * mm});
            skLineSegment(sketch, "E384", {"start": v(-9.87, -5.14) * mm, "end": v(-10.16, -5.78) * mm});
            skLineSegment(sketch, "E385", {"start": v(-10.16, -5.78) * mm, "end": v(-9.19, -6.22) * mm});
            skLineSegment(sketch, "E386", {"start": v(-15.07, 11.08) * mm, "end": v(-11.3, 11.08) * mm});
            skLineSegment(sketch, "E387", {"start": v(-11.3, 11.08) * mm, "end": v(-11.3, 1.23) * mm});
            skLineSegment(sketch, "E388", {"start": v(-11.3, 1.23) * mm, "end": v(-11.12, 1.23) * mm});
            skLineSegment(sketch, "E389", {"start": v(-11.12, 1.23) * mm, "end": v(-11.12, 11.08) * mm});
            skLineSegment(sketch, "E390", {"start": v(-11.12, 11.08) * mm, "end": v(-6.5, 11.08) * mm});
            skLineSegment(sketch, "E391", {"start": v(-6.5, 11.08) * mm, "end": v(-5.56, 11) * mm});
            skLineSegment(sketch, "E392", {"start": v(-5.56, 11) * mm, "end": v(-4.7, 10.73) * mm});
            skLineSegment(sketch, "E393", {"start": v(-4.7, 10.73) * mm, "end": v(-3.97, 10.3) * mm});
            skLineSegment(sketch, "E394", {"start": v(-3.97, 10.3) * mm, "end": v(-3.34, 9.73) * mm});
            skLineSegment(sketch, "E395", {"start": v(-3.34, 9.73) * mm, "end": v(-2.84, 9.02) * mm});
            skLineSegment(sketch, "E396", {"start": v(-2.84, 9.02) * mm, "end": v(-2.47, 8.2) * mm});
            skLineSegment(sketch, "E397", {"start": v(-2.47, 8.2) * mm, "end": v(-2.47, 8.2) * mm});
            skLineSegment(sketch, "E398", {"start": v(-2.47, 8.2) * mm, "end": v(-2.24, 7.25) * mm});
            skLineSegment(sketch, "E399", {"start": v(-2.24, 7.25) * mm, "end": v(-2.17, 6.2) * mm});
            skLineSegment(sketch, "E400", {"start": v(-2.17, 6.2) * mm, "end": v(-2.24, 5.2) * mm});
            skLineSegment(sketch, "E401", {"start": v(-2.24, 5.2) * mm, "end": v(-2.47, 4.26) * mm});
            skLineSegment(sketch, "E402", {"start": v(-2.47, 4.26) * mm, "end": v(-2.47, 4.26) * mm});
            skLineSegment(sketch, "E403", {"start": v(-2.47, 4.26) * mm, "end": v(-2.84, 3.44) * mm});
            skLineSegment(sketch, "E404", {"start": v(-2.84, 3.44) * mm, "end": v(-3.34, 2.72) * mm});
            skLineSegment(sketch, "E405", {"start": v(-3.34, 2.72) * mm, "end": v(-3.97, 2.14) * mm});
            skLineSegment(sketch, "E406", {"start": v(-3.97, 2.14) * mm, "end": v(-4.72, 1.7) * mm});
            skLineSegment(sketch, "E407", {"start": v(-4.72, 1.7) * mm, "end": v(-4.72, 1.7) * mm});
            skLineSegment(sketch, "E408", {"start": v(-4.72, 1.7) * mm, "end": v(-5.58, 1.44) * mm});
            skLineSegment(sketch, "E409", {"start": v(-5.58, 1.44) * mm, "end": v(-6.51, 1.34) * mm});
            skLineSegment(sketch, "E410", {"start": v(-6.51, 1.34) * mm, "end": v(-6.94, 1.34) * mm});
            skLineSegment(sketch, "E411", {"start": v(-6.94, 1.34) * mm, "end": v(-6.94, -3.35) * mm});
            skLineSegment(sketch, "E412", {"start": v(-6.94, -3.35) * mm, "end": v(-7.53, -3.35) * mm});
            skLineSegment(sketch, "E413", {"start": v(-7.53, -3.35) * mm, "end": v(-5.27, -11.08) * mm});
            skLineSegment(sketch, "E414", {"start": v(-5.27, -11.08) * mm, "end": v(-8.71, -11.08) * mm});
            skLineSegment(sketch, "E415", {"start": v(-8.71, -11.08) * mm, "end": v(-9.8, -7.94) * mm});
            skLineSegment(sketch, "E416", {"start": v(-9.8, -7.94) * mm, "end": v(-11.85, -7.94) * mm});
            skLineSegment(sketch, "E417", {"start": v(-11.85, -7.94) * mm, "end": v(-12.91, -11.08) * mm});
            skLineSegment(sketch, "E418", {"start": v(-12.91, -11.08) * mm, "end": v(-16.35, -11.08) * mm});
            skLineSegment(sketch, "E419", {"start": v(-16.35, -11.08) * mm, "end": v(-14.09, -3.35) * mm});
            skLineSegment(sketch, "E420", {"start": v(-14.09, -3.35) * mm, "end": v(-15.4, -3.35) * mm});
            skLineSegment(sketch, "E421", {"start": v(-15.4, -3.35) * mm, "end": v(-15.4, 11.08) * mm});
            skLineSegment(sketch, "E422", {"start": v(-15.4, 11.08) * mm, "end": v(-15.07, 11.08) * mm});
            skLineSegment(sketch, "E423", {"start": v(-11.97, 10.4) * mm, "end": v(-14.73, 10.4) * mm});
            skLineSegment(sketch, "E424", {"start": v(-14.73, 10.4) * mm, "end": v(-14.73, -2.67) * mm});
            skLineSegment(sketch, "E425", {"start": v(-14.73, -2.67) * mm, "end": v(-13.89, -2.67) * mm});
            skLineSegment(sketch, "E426", {"start": v(-13.89, -2.67) * mm, "end": v(-12.75, 1.23) * mm});
            skLineSegment(sketch, "E427", {"start": v(-12.75, 1.23) * mm, "end": v(-11.97, 1.23) * mm});
            skLineSegment(sketch, "E428", {"start": v(-11.97, 1.23) * mm, "end": v(-11.97, 10.4) * mm});
            skLineSegment(sketch, "E429", {"start": v(39.93, 1.23) * mm, "end": v(39.93, -11.08) * mm});
            skLineSegment(sketch, "E430", {"start": v(39.93, -11.08) * mm, "end": v(36.88, -11.08) * mm});
            skLineSegment(sketch, "E431", {"start": v(36.88, -11.08) * mm, "end": v(34, -5.79) * mm});
            skLineSegment(sketch, "E432", {"start": v(34, -5.79) * mm, "end": v(34, -11.08) * mm});
            skLineSegment(sketch, "E433", {"start": v(34, -11.08) * mm, "end": v(30.77, -11.08) * mm});
            skLineSegment(sketch, "E434", {"start": v(30.77, -11.08) * mm, "end": v(30.77, 1.23) * mm});
            skLineSegment(sketch, "E435", {"start": v(30.77, 1.23) * mm, "end": v(30.8, 1.23) * mm});
            skLineSegment(sketch, "E436", {"start": v(30.8, 1.23) * mm, "end": v(30.8, 11.08) * mm});
            skLineSegment(sketch, "E437", {"start": v(30.8, 11.08) * mm, "end": v(40.07, 11.08) * mm});
            skLineSegment(sketch, "E438", {"start": v(40.07, 11.08) * mm, "end": v(40.07, 6.96) * mm});
            skLineSegment(sketch, "E439", {"start": v(40.07, 6.96) * mm, "end": v(34.92, 6.96) * mm});
            skLineSegment(sketch, "E440", {"start": v(34.92, 6.96) * mm, "end": v(34.92, 5.93) * mm});
            skLineSegment(sketch, "E441", {"start": v(34.92, 5.93) * mm, "end": v(38.7, 5.93) * mm});
            skLineSegment(sketch, "E442", {"start": v(38.7, 5.93) * mm, "end": v(38.7, 1.8) * mm});
            skLineSegment(sketch, "E443", {"start": v(38.7, 1.8) * mm, "end": v(34.92, 1.8) * mm});
            skLineSegment(sketch, "E444", {"start": v(34.92, 1.8) * mm, "end": v(34.92, 0.76) * mm});
            skLineSegment(sketch, "E445", {"start": v(34.92, 0.76) * mm, "end": v(36.69, 0.76) * mm});
            skLineSegment(sketch, "E446", {"start": v(36.69, 0.76) * mm, "end": v(36.69, 1.23) * mm});
            skLineSegment(sketch, "E447", {"start": v(36.69, 1.23) * mm, "end": v(39.93, 1.23) * mm});
            skLineSegment(sketch, "E448", {"start": v(31.48, 1.23) * mm, "end": v(33.82, 1.23) * mm});
            skLineSegment(sketch, "E449", {"start": v(33.82, 1.23) * mm, "end": v(34.24, 0.46) * mm});
            skLineSegment(sketch, "E450", {"start": v(34.24, 0.46) * mm, "end": v(34.24, 2.48) * mm});
            skLineSegment(sketch, "E451", {"start": v(34.24, 2.48) * mm, "end": v(38.03, 2.48) * mm});
            skLineSegment(sketch, "E452", {"start": v(38.03, 2.48) * mm, "end": v(38.03, 5.25) * mm});
            skLineSegment(sketch, "E453", {"start": v(38.03, 5.25) * mm, "end": v(34.24, 5.25) * mm});
            skLineSegment(sketch, "E454", {"start": v(34.24, 5.25) * mm, "end": v(34.24, 5.59) * mm});
            skLineSegment(sketch, "E455", {"start": v(34.24, 5.59) * mm, "end": v(34.24, 7.64) * mm});
            skLineSegment(sketch, "E456", {"start": v(34.24, 7.64) * mm, "end": v(39.4, 7.64) * mm});
            skLineSegment(sketch, "E457", {"start": v(39.4, 7.64) * mm, "end": v(39.4, 10.4) * mm});
            skLineSegment(sketch, "E458", {"start": v(39.4, 10.4) * mm, "end": v(31.48, 10.4) * mm});
            skLineSegment(sketch, "E459", {"start": v(31.48, 10.4) * mm, "end": v(31.48, 1.23) * mm});
            skLineSegment(sketch, "E460", {"start": v(34.44, 0.09) * mm, "end": v(35.94, -2.67) * mm});
            skLineSegment(sketch, "E461", {"start": v(35.94, -2.67) * mm, "end": v(36.69, -2.67) * mm});
            skLineSegment(sketch, "E462", {"start": v(36.69, -2.67) * mm, "end": v(36.69, 0.09) * mm});
            skLineSegment(sketch, "E463", {"start": v(36.69, 0.09) * mm, "end": v(34.44, 0.09) * mm});
            skLineSegment(sketch, "E464", {"start": v(36.3, -3.35) * mm, "end": v(36.69, -4.06) * mm});
            skLineSegment(sketch, "E465", {"start": v(36.69, -4.06) * mm, "end": v(36.69, -3.35) * mm});
            skLineSegment(sketch, "E466", {"start": v(36.69, -3.35) * mm, "end": v(36.3, -3.35) * mm});
            skSolve(sketch);
        }
        {
            var Q0;
            Q0 = qSketchRegion(id + "F0", true);
            extrude(context, id + "F1", {"entities" : qUnion([Q0]), "depth" : 5 * mm, "offsetDistance" : 25 * mm});
        }
        {
            var Q0;
            Q0=qCreatedBy(makeId("Right.planeOp"),FACE);
            var sketch = newSketch(context, id + "F2", { "sketchPlane" : qUnion([Q0])});
            skLineSegment(sketch, "E467", {"start": v(0, 0) * mm, "end": v(3.75, 0) * mm});
            skLineSegment(sketch, "E468", {"start": v(3.75, 0) * mm, "end": v(0, 1.8) * mm});
            skLineSegment(sketch, "E469", {"start": v(0, 1.8) * mm, "end": v(-3.75, 0) * mm});
            skLineSegment(sketch, "E470", {"start": v(-3.75, 0) * mm, "end": v(0, 0) * mm});
            skSolve(sketch);
        }
        {
            var Q0;
            Q0 = qSketchRegion(id + "F2", true);
            extrude(context, id + "F3", {"entities" : qUnion([Q0]), "depth" : 35 * mm, "offsetDistance" : 25 * mm, "hasSecondDirection" : true, "secondDirectionOppositeDirection" : true, "secondDirectionDepth" : 23 * mm});
        }
        {
            var Q0;
            Q0=qCreatedBy(makeId("Top.planeOp"),FACE);
            var sketch = newSketch(context, id + "F4", { "sketchPlane" : qUnion([Q0])});
            skLineSegment(sketch, "E471.bottom", {"start": v(35, -4) * mm, "end": v(-23, -4) * mm});
            skLineSegment(sketch, "E471.top", {"start": v(35, 4) * mm, "end": v(-23, 4) * mm});
            skLineSegment(sketch, "E471.left", {"start": v(37, -2) * mm, "end": v(37, 2) * mm});
            skLineSegment(sketch, "E471.right", {"start": v(-25, -2) * mm, "end": v(-25, 2) * mm});
            skPoint(sketch, "E471.middle", {"position": v(0, 0) * mm});
            skPoint(sketch, "E472.visualSharp", {"position": v(-25, 4) * mm});
            skArc(sketch, "E472.filletArc", {"start": v(-23, 4) * mm, "mid": v(-24.41, 3.41) * mm, "end": v(-25, 2) * mm});
            skPoint(sketch, "E473.visualSharp", {"position": v(-25, -4) * mm});
            skArc(sketch, "E473.filletArc", {"start": v(-25, -2) * mm, "mid": v(-24.41, -3.41) * mm, "end": v(-23, -4) * mm});
            skPoint(sketch, "E474.visualSharp", {"position": v(37, -4) * mm});
            skArc(sketch, "E474.filletArc", {"start": v(35, -4) * mm, "mid": v(36.41, -3.41) * mm, "end": v(37, -2) * mm});
            skPoint(sketch, "E475.visualSharp", {"position": v(37, 4) * mm});
            skArc(sketch, "E475.filletArc", {"start": v(37, 2) * mm, "mid": v(36.41, 3.41) * mm, "end": v(35, 4) * mm});
            skSolve(sketch);
        }
        {
            var Q0;
            Q0 = qSketchRegion(id + "F4", true);
            extrude(context, id + "F5", {"entities" : qUnion([Q0]), "depth" : 1 * mm, "offsetDistance" : 25 * mm});
        }
        {
            var Q0;
            Q0=makeQuery(id+"F3.opExtrude","SWEPT_BODY",BODY,{"disambiguationData":[OSD([sQuery(id+"F2.wireOp",EDGE,"E467"),sQuery(id+"F2.wireOp",EDGE,"E468"),sQuery(id+"F2.wireOp",EDGE,"E469"),sQuery(id+"F2.wireOp",EDGE,"E470")])]});
            var Q1;
            Q1=makeQuery(id+"F5.opExtrude","SWEPT_BODY",BODY,{"disambiguationData":[OSD([sQuery(id+"F4.wireOp",EDGE,"E471.bottom"),sQuery(id+"F4.wireOp",EDGE,"E471.top"),sQuery(id+"F4.wireOp",EDGE,"E471.left"),sQuery(id+"F4.wireOp",EDGE,"E471.right"),sQuery(id+"F4.wireOp",EDGE,"E472.filletArc"),sQuery(id+"F4.wireOp",EDGE,"E473.filletArc"),sQuery(id+"F4.wireOp",EDGE,"E474.filletArc"),sQuery(id+"F4.wireOp",EDGE,"E475.filletArc")])]});
            booleanBodies(context, id + "F6", {"operationType" : BooleanOperationType.UNION, "tools" : qUnion([Q0, Q1])});
        }
        {
            var Q0;
            {var subQ0=makeQuery(id+"F3.opExtrude","SWEPT_FACE",FACE,{"disambiguationData":[OSD([sQuery(id+"F2.wireOp",EDGE,"E468")])]});var subQ1=makeQuery(id+"F5.opExtrude","CAP_FACE",FACE,{"disambiguationData":[OSD([sQuery(id+"F4.wireOp",EDGE,"E471.bottom"),sQuery(id+"F4.wireOp",EDGE,"E471.top"),sQuery(id+"F4.wireOp",EDGE,"E471.left"),sQuery(id+"F4.wireOp",EDGE,"E471.right"),sQuery(id+"F4.wireOp",EDGE,"E472.filletArc"),sQuery(id+"F4.wireOp",EDGE,"E473.filletArc"),sQuery(id+"F4.wireOp",EDGE,"E474.filletArc"),sQuery(id+"F4.wireOp",EDGE,"E475.filletArc")])],"isStart":false});Q0=makeQuery(id+"F18.opBoolean","SPLIT",EDGE,{"disambiguationData":[TD([makeQuery(id+"F1.opExtrude","SWEPT_FACE",FACE,{"disambiguationData":[OSD([sQuery(id+"F0.wireOp",EDGE,"E421")])]})])],"derivedFrom":makeQuery(id+"F6.opBoolean","INTERSECT",EDGE,{"derivedFrom":[subQ0,subQ1]})});}
            var Q1;
            {var subQ0=makeQuery(id+"F3.opExtrude","SWEPT_FACE",FACE,{"disambiguationData":[OSD([sQuery(id+"F2.wireOp",EDGE,"E469")])]});var subQ1=makeQuery(id+"F5.opExtrude","CAP_FACE",FACE,{"disambiguationData":[OSD([sQuery(id+"F4.wireOp",EDGE,"E471.bottom"),sQuery(id+"F4.wireOp",EDGE,"E471.top"),sQuery(id+"F4.wireOp",EDGE,"E471.left"),sQuery(id+"F4.wireOp",EDGE,"E471.right"),sQuery(id+"F4.wireOp",EDGE,"E472.filletArc"),sQuery(id+"F4.wireOp",EDGE,"E473.filletArc"),sQuery(id+"F4.wireOp",EDGE,"E474.filletArc"),sQuery(id+"F4.wireOp",EDGE,"E475.filletArc")])],"isStart":false});Q1=makeQuery(id+"F18.opBoolean","SPLIT",EDGE,{"disambiguationData":[TD([makeQuery(id+"F1.opExtrude","SWEPT_FACE",FACE,{"disambiguationData":[OSD([sQuery(id+"F0.wireOp",EDGE,"E216")])]})])],"derivedFrom":makeQuery(id+"F6.opBoolean","INTERSECT",EDGE,{"derivedFrom":[subQ0,subQ1]})});}
            fillet(context, id + "F7", {"entities" : qUnion([Q0, Q1]), "radius" : 5 * mm, "tangentPropagation" : true, "allowEdgeOverflow" : false});
        }
        {
            var Q0;
            {var subQ0=sQuery(id+"F2.wireOp",EDGE,"E468");var subQ1=sQuery(id+"F2.wireOp",EDGE,"E469");Q0=makeQuery(id+"F18.opBoolean","SPLIT",EDGE,{"disambiguationData":[TD([makeQuery(id+"F1.opExtrude","SWEPT_FACE",FACE,{"disambiguationData":[OSD([sQuery(id+"F0.wireOp",EDGE,"E216")])]})])],"derivedFrom":makeQuery(id+"F3.opExtrude","SWEPT_EDGE",EDGE,{"disambiguationData":[OSD([subQ0,subQ1])]})});}
            fillet(context, id + "F8", {"entities" : qUnion([Q0]), "radius" : 1 * mm, "tangentPropagation" : true, "allowEdgeOverflow" : false});
        }
        {
            var Q0;
            Q0=qCreatedBy(makeId("Right.planeOp"),FACE);
            var sketch = newSketch(context, id + "F9", { "sketchPlane" : qUnion([Q0])});
            skLineSegment(sketch, "E476", {"start": v(0, -0.96) * mm, "end": v(-7, -0.96) * mm, "construction": true});
            skLineSegment(sketch, "E477", {"start": v(0, -0.96) * mm, "end": v(7, -0.96) * mm, "construction": true});
            skArc(sketch, "E478", {"start": v(7, -0.96) * mm, "mid": v(0, 1.96) * mm, "end": v(-7, -0.96) * mm});
            skLineSegment(sketch, "E479", {"start": v(-7, -0.96) * mm, "end": v(-7, 3.68) * mm});
            skLineSegment(sketch, "E480", {"start": v(-7, 3.68) * mm, "end": v(7, 3.68) * mm});
            skLineSegment(sketch, "E481", {"start": v(7, 3.68) * mm, "end": v(7, -0.96) * mm});
            skSolve(sketch);
        }
        {
            var Q0;
            Q0=makeQuery(id+"F1.opExtrude","SWEPT_BODY",BODY,{"disambiguationData":[OSD([sQuery(id+"F0.wireOp",EDGE,"E211"),sQuery(id+"F0.wireOp",EDGE,"E212"),sQuery(id+"F0.wireOp",EDGE,"E213"),sQuery(id+"F0.wireOp",EDGE,"E214"),sQuery(id+"F0.wireOp",EDGE,"E215"),sQuery(id+"F0.wireOp",EDGE,"E216"),sQuery(id+"F0.wireOp",EDGE,"E217"),sQuery(id+"F0.wireOp",EDGE,"E218"),sQuery(id+"F0.wireOp",EDGE,"E219"),sQuery(id+"F0.wireOp",EDGE,"E220"),sQuery(id+"F0.wireOp",EDGE,"E221"),sQuery(id+"F0.wireOp",EDGE,"E222"),sQuery(id+"F0.wireOp",EDGE,"E223"),sQuery(id+"F0.wireOp",EDGE,"E224"),sQuery(id+"F0.wireOp",EDGE,"E225"),sQuery(id+"F0.wireOp",EDGE,"E226"),sQuery(id+"F0.wireOp",EDGE,"E227"),sQuery(id+"F0.wireOp",EDGE,"E228"),sQuery(id+"F0.wireOp",EDGE,"E229"),sQuery(id+"F0.wireOp",EDGE,"E230"),sQuery(id+"F0.wireOp",EDGE,"E231"),sQuery(id+"F0.wireOp",EDGE,"E232"),sQuery(id+"F0.wireOp",EDGE,"E233"),sQuery(id+"F0.wireOp",EDGE,"E234"),sQuery(id+"F0.wireOp",EDGE,"E235"),sQuery(id+"F0.wireOp",EDGE,"E236"),sQuery(id+"F0.wireOp",EDGE,"E237"),sQuery(id+"F0.wireOp",EDGE,"E238"),sQuery(id+"F0.wireOp",EDGE,"E239"),sQuery(id+"F0.wireOp",EDGE,"E240"),sQuery(id+"F0.wireOp",EDGE,"E241"),sQuery(id+"F0.wireOp",EDGE,"E242"),sQuery(id+"F0.wireOp",EDGE,"E243"),sQuery(id+"F0.wireOp",EDGE,"E244"),sQuery(id+"F0.wireOp",EDGE,"E245"),sQuery(id+"F0.wireOp",EDGE,"E246"),sQuery(id+"F0.wireOp",EDGE,"E247"),sQuery(id+"F0.wireOp",EDGE,"E248"),sQuery(id+"F0.wireOp",EDGE,"E249"),sQuery(id+"F0.wireOp",EDGE,"E250"),sQuery(id+"F0.wireOp",EDGE,"E251"),sQuery(id+"F0.wireOp",EDGE,"E252"),sQuery(id+"F0.wireOp",EDGE,"E253"),sQuery(id+"F0.wireOp",EDGE,"E254"),sQuery(id+"F0.wireOp",EDGE,"E255"),sQuery(id+"F0.wireOp",EDGE,"E256"),sQuery(id+"F0.wireOp",EDGE,"E257"),sQuery(id+"F0.wireOp",EDGE,"E258")])]});
            var Q1;
            Q1=makeQuery(id+"F1.opExtrude","SWEPT_BODY",BODY,{"disambiguationData":[OSD([sQuery(id+"F0.wireOp",EDGE,"E259"),sQuery(id+"F0.wireOp",EDGE,"E260"),sQuery(id+"F0.wireOp",EDGE,"E261"),sQuery(id+"F0.wireOp",EDGE,"E262"),sQuery(id+"F0.wireOp",EDGE,"E263"),sQuery(id+"F0.wireOp",EDGE,"E264"),sQuery(id+"F0.wireOp",EDGE,"E265"),sQuery(id+"F0.wireOp",EDGE,"E266"),sQuery(id+"F0.wireOp",EDGE,"E267"),sQuery(id+"F0.wireOp",EDGE,"E268"),sQuery(id+"F0.wireOp",EDGE,"E269"),sQuery(id+"F0.wireOp",EDGE,"E270")])]});
            var Q2;
            Q2=makeQuery(id+"F1.opExtrude","SWEPT_BODY",BODY,{"disambiguationData":[OSD([sQuery(id+"F0.wireOp",EDGE,"E271"),sQuery(id+"F0.wireOp",EDGE,"E272"),sQuery(id+"F0.wireOp",EDGE,"E273"),sQuery(id+"F0.wireOp",EDGE,"E274"),sQuery(id+"F0.wireOp",EDGE,"E275"),sQuery(id+"F0.wireOp",EDGE,"E276"),sQuery(id+"F0.wireOp",EDGE,"E277"),sQuery(id+"F0.wireOp",EDGE,"E278"),sQuery(id+"F0.wireOp",EDGE,"E279"),sQuery(id+"F0.wireOp",EDGE,"E280"),sQuery(id+"F0.wireOp",EDGE,"E281"),sQuery(id+"F0.wireOp",EDGE,"E282"),sQuery(id+"F0.wireOp",EDGE,"E283"),sQuery(id+"F0.wireOp",EDGE,"E284"),sQuery(id+"F0.wireOp",EDGE,"E285"),sQuery(id+"F0.wireOp",EDGE,"E286"),sQuery(id+"F0.wireOp",EDGE,"E287"),sQuery(id+"F0.wireOp",EDGE,"E288"),sQuery(id+"F0.wireOp",EDGE,"E289"),sQuery(id+"F0.wireOp",EDGE,"E290"),sQuery(id+"F0.wireOp",EDGE,"E291"),sQuery(id+"F0.wireOp",EDGE,"E292"),sQuery(id+"F0.wireOp",EDGE,"E293"),sQuery(id+"F0.wireOp",EDGE,"E294"),sQuery(id+"F0.wireOp",EDGE,"E295"),sQuery(id+"F0.wireOp",EDGE,"E296"),sQuery(id+"F0.wireOp",EDGE,"E297"),sQuery(id+"F0.wireOp",EDGE,"E298"),sQuery(id+"F0.wireOp",EDGE,"E299"),sQuery(id+"F0.wireOp",EDGE,"E300"),sQuery(id+"F0.wireOp",EDGE,"E301"),sQuery(id+"F0.wireOp",EDGE,"E302"),sQuery(id+"F0.wireOp",EDGE,"E303"),sQuery(id+"F0.wireOp",EDGE,"E304"),sQuery(id+"F0.wireOp",EDGE,"E305"),sQuery(id+"F0.wireOp",EDGE,"E306"),sQuery(id+"F0.wireOp",EDGE,"E307"),sQuery(id+"F0.wireOp",EDGE,"E308"),sQuery(id+"F0.wireOp",EDGE,"E309"),sQuery(id+"F0.wireOp",EDGE,"E310"),sQuery(id+"F0.wireOp",EDGE,"E311")])]});
            var Q3;
            Q3=makeQuery(id+"F1.opExtrude","SWEPT_BODY",BODY,{"disambiguationData":[OSD([sQuery(id+"F0.wireOp",EDGE,"E312"),sQuery(id+"F0.wireOp",EDGE,"E313"),sQuery(id+"F0.wireOp",EDGE,"E314"),sQuery(id+"F0.wireOp",EDGE,"E315"),sQuery(id+"F0.wireOp",EDGE,"E316"),sQuery(id+"F0.wireOp",EDGE,"E317"),sQuery(id+"F0.wireOp",EDGE,"E318"),sQuery(id+"F0.wireOp",EDGE,"E319"),sQuery(id+"F0.wireOp",EDGE,"E320"),sQuery(id+"F0.wireOp",EDGE,"E321"),sQuery(id+"F0.wireOp",EDGE,"E322"),sQuery(id+"F0.wireOp",EDGE,"E323"),sQuery(id+"F0.wireOp",EDGE,"E324"),sQuery(id+"F0.wireOp",EDGE,"E325"),sQuery(id+"F0.wireOp",EDGE,"E326"),sQuery(id+"F0.wireOp",EDGE,"E327"),sQuery(id+"F0.wireOp",EDGE,"E328"),sQuery(id+"F0.wireOp",EDGE,"E329"),sQuery(id+"F0.wireOp",EDGE,"E330"),sQuery(id+"F0.wireOp",EDGE,"E331"),sQuery(id+"F0.wireOp",EDGE,"E332"),sQuery(id+"F0.wireOp",EDGE,"E333"),sQuery(id+"F0.wireOp",EDGE,"E334"),sQuery(id+"F0.wireOp",EDGE,"E335"),sQuery(id+"F0.wireOp",EDGE,"E336"),sQuery(id+"F0.wireOp",EDGE,"E337"),sQuery(id+"F0.wireOp",EDGE,"E338"),sQuery(id+"F0.wireOp",EDGE,"E339"),sQuery(id+"F0.wireOp",EDGE,"E340"),sQuery(id+"F0.wireOp",EDGE,"E341"),sQuery(id+"F0.wireOp",EDGE,"E342"),sQuery(id+"F0.wireOp",EDGE,"E343"),sQuery(id+"F0.wireOp",EDGE,"E344"),sQuery(id+"F0.wireOp",EDGE,"E345"),sQuery(id+"F0.wireOp",EDGE,"E346"),sQuery(id+"F0.wireOp",EDGE,"E347"),sQuery(id+"F0.wireOp",EDGE,"E348"),sQuery(id+"F0.wireOp",EDGE,"E349"),sQuery(id+"F0.wireOp",EDGE,"E350"),sQuery(id+"F0.wireOp",EDGE,"E351"),sQuery(id+"F0.wireOp",EDGE,"E352"),sQuery(id+"F0.wireOp",EDGE,"E353"),sQuery(id+"F0.wireOp",EDGE,"E354"),sQuery(id+"F0.wireOp",EDGE,"E355"),sQuery(id+"F0.wireOp",EDGE,"E356"),sQuery(id+"F0.wireOp",EDGE,"E357"),sQuery(id+"F0.wireOp",EDGE,"E358"),sQuery(id+"F0.wireOp",EDGE,"E359"),sQuery(id+"F0.wireOp",EDGE,"E360"),sQuery(id+"F0.wireOp",EDGE,"E361"),sQuery(id+"F0.wireOp",EDGE,"E362"),sQuery(id+"F0.wireOp",EDGE,"E363"),sQuery(id+"F0.wireOp",EDGE,"E364"),sQuery(id+"F0.wireOp",EDGE,"E365"),sQuery(id+"F0.wireOp",EDGE,"E366"),sQuery(id+"F0.wireOp",EDGE,"E367"),sQuery(id+"F0.wireOp",EDGE,"E368"),sQuery(id+"F0.wireOp",EDGE,"E369"),sQuery(id+"F0.wireOp",EDGE,"E370"),sQuery(id+"F0.wireOp",EDGE,"E371"),sQuery(id+"F0.wireOp",EDGE,"E372"),sQuery(id+"F0.wireOp",EDGE,"E373"),sQuery(id+"F0.wireOp",EDGE,"E374"),sQuery(id+"F0.wireOp",EDGE,"E375"),sQuery(id+"F0.wireOp",EDGE,"E376"),sQuery(id+"F0.wireOp",EDGE,"E377"),sQuery(id+"F0.wireOp",EDGE,"E378"),sQuery(id+"F0.wireOp",EDGE,"E379"),sQuery(id+"F0.wireOp",EDGE,"E380"),sQuery(id+"F0.wireOp",EDGE,"E381"),sQuery(id+"F0.wireOp",EDGE,"E382"),sQuery(id+"F0.wireOp",EDGE,"E383"),sQuery(id+"F0.wireOp",EDGE,"E384"),sQuery(id+"F0.wireOp",EDGE,"E385"),sQuery(id+"F0.wireOp",EDGE,"E386"),sQuery(id+"F0.wireOp",EDGE,"E387"),sQuery(id+"F0.wireOp",EDGE,"E388"),sQuery(id+"F0.wireOp",EDGE,"E389"),sQuery(id+"F0.wireOp",EDGE,"E390"),sQuery(id+"F0.wireOp",EDGE,"E391"),sQuery(id+"F0.wireOp",EDGE,"E392"),sQuery(id+"F0.wireOp",EDGE,"E393"),sQuery(id+"F0.wireOp",EDGE,"E394"),sQuery(id+"F0.wireOp",EDGE,"E395"),sQuery(id+"F0.wireOp",EDGE,"E396"),sQuery(id+"F0.wireOp",EDGE,"E397"),sQuery(id+"F0.wireOp",EDGE,"E398"),sQuery(id+"F0.wireOp",EDGE,"E399"),sQuery(id+"F0.wireOp",EDGE,"E400"),sQuery(id+"F0.wireOp",EDGE,"E401"),sQuery(id+"F0.wireOp",EDGE,"E402"),sQuery(id+"F0.wireOp",EDGE,"E403"),sQuery(id+"F0.wireOp",EDGE,"E404"),sQuery(id+"F0.wireOp",EDGE,"E405"),sQuery(id+"F0.wireOp",EDGE,"E406"),sQuery(id+"F0.wireOp",EDGE,"E407"),sQuery(id+"F0.wireOp",EDGE,"E408"),sQuery(id+"F0.wireOp",EDGE,"E409"),sQuery(id+"F0.wireOp",EDGE,"E410"),sQuery(id+"F0.wireOp",EDGE,"E411"),sQuery(id+"F0.wireOp",EDGE,"E412"),sQuery(id+"F0.wireOp",EDGE,"E413"),sQuery(id+"F0.wireOp",EDGE,"E414"),sQuery(id+"F0.wireOp",EDGE,"E415"),sQuery(id+"F0.wireOp",EDGE,"E416"),sQuery(id+"F0.wireOp",EDGE,"E417"),sQuery(id+"F0.wireOp",EDGE,"E418"),sQuery(id+"F0.wireOp",EDGE,"E419"),sQuery(id+"F0.wireOp",EDGE,"E420"),sQuery(id+"F0.wireOp",EDGE,"E421"),sQuery(id+"F0.wireOp",EDGE,"E422"),sQuery(id+"F0.wireOp",EDGE,"E423"),sQuery(id+"F0.wireOp",EDGE,"E424"),sQuery(id+"F0.wireOp",EDGE,"E425"),sQuery(id+"F0.wireOp",EDGE,"E426"),sQuery(id+"F0.wireOp",EDGE,"E427"),sQuery(id+"F0.wireOp",EDGE,"E428")])]});
            var Q4;
            Q4=makeQuery(id+"F1.opExtrude","SWEPT_BODY",BODY,{"disambiguationData":[OSD([sQuery(id+"F0.wireOp",EDGE,"E0"),sQuery(id+"F0.wireOp",EDGE,"E1"),sQuery(id+"F0.wireOp",EDGE,"E2"),sQuery(id+"F0.wireOp",EDGE,"E3"),sQuery(id+"F0.wireOp",EDGE,"E4"),sQuery(id+"F0.wireOp",EDGE,"E5"),sQuery(id+"F0.wireOp",EDGE,"E6"),sQuery(id+"F0.wireOp",EDGE,"E7"),sQuery(id+"F0.wireOp",EDGE,"E8"),sQuery(id+"F0.wireOp",EDGE,"E9"),sQuery(id+"F0.wireOp",EDGE,"E10"),sQuery(id+"F0.wireOp",EDGE,"E11"),sQuery(id+"F0.wireOp",EDGE,"E12"),sQuery(id+"F0.wireOp",EDGE,"E13"),sQuery(id+"F0.wireOp",EDGE,"E14"),sQuery(id+"F0.wireOp",EDGE,"E15"),sQuery(id+"F0.wireOp",EDGE,"E16"),sQuery(id+"F0.wireOp",EDGE,"E17"),sQuery(id+"F0.wireOp",EDGE,"E18"),sQuery(id+"F0.wireOp",EDGE,"E19"),sQuery(id+"F0.wireOp",EDGE,"E20"),sQuery(id+"F0.wireOp",EDGE,"E21"),sQuery(id+"F0.wireOp",EDGE,"E22"),sQuery(id+"F0.wireOp",EDGE,"E23"),sQuery(id+"F0.wireOp",EDGE,"E24"),sQuery(id+"F0.wireOp",EDGE,"E25"),sQuery(id+"F0.wireOp",EDGE,"E26"),sQuery(id+"F0.wireOp",EDGE,"E27"),sQuery(id+"F0.wireOp",EDGE,"E28"),sQuery(id+"F0.wireOp",EDGE,"E29"),sQuery(id+"F0.wireOp",EDGE,"E30"),sQuery(id+"F0.wireOp",EDGE,"E31"),sQuery(id+"F0.wireOp",EDGE,"E32"),sQuery(id+"F0.wireOp",EDGE,"E33"),sQuery(id+"F0.wireOp",EDGE,"E34"),sQuery(id+"F0.wireOp",EDGE,"E35"),sQuery(id+"F0.wireOp",EDGE,"E36"),sQuery(id+"F0.wireOp",EDGE,"E37"),sQuery(id+"F0.wireOp",EDGE,"E38"),sQuery(id+"F0.wireOp",EDGE,"E39"),sQuery(id+"F0.wireOp",EDGE,"E40"),sQuery(id+"F0.wireOp",EDGE,"E41"),sQuery(id+"F0.wireOp",EDGE,"E42"),sQuery(id+"F0.wireOp",EDGE,"E43"),sQuery(id+"F0.wireOp",EDGE,"E44"),sQuery(id+"F0.wireOp",EDGE,"E45"),sQuery(id+"F0.wireOp",EDGE,"E46"),sQuery(id+"F0.wireOp",EDGE,"E47"),sQuery(id+"F0.wireOp",EDGE,"E48"),sQuery(id+"F0.wireOp",EDGE,"E49"),sQuery(id+"F0.wireOp",EDGE,"E50"),sQuery(id+"F0.wireOp",EDGE,"E51"),sQuery(id+"F0.wireOp",EDGE,"E52"),sQuery(id+"F0.wireOp",EDGE,"E53"),sQuery(id+"F0.wireOp",EDGE,"E54"),sQuery(id+"F0.wireOp",EDGE,"E55"),sQuery(id+"F0.wireOp",EDGE,"E56"),sQuery(id+"F0.wireOp",EDGE,"E57"),sQuery(id+"F0.wireOp",EDGE,"E58"),sQuery(id+"F0.wireOp",EDGE,"E59"),sQuery(id+"F0.wireOp",EDGE,"E60"),sQuery(id+"F0.wireOp",EDGE,"E61"),sQuery(id+"F0.wireOp",EDGE,"E62"),sQuery(id+"F0.wireOp",EDGE,"E63"),sQuery(id+"F0.wireOp",EDGE,"E64"),sQuery(id+"F0.wireOp",EDGE,"E65"),sQuery(id+"F0.wireOp",EDGE,"E66"),sQuery(id+"F0.wireOp",EDGE,"E67"),sQuery(id+"F0.wireOp",EDGE,"E68"),sQuery(id+"F0.wireOp",EDGE,"E69"),sQuery(id+"F0.wireOp",EDGE,"E70"),sQuery(id+"F0.wireOp",EDGE,"E71"),sQuery(id+"F0.wireOp",EDGE,"E72"),sQuery(id+"F0.wireOp",EDGE,"E73"),sQuery(id+"F0.wireOp",EDGE,"E74"),sQuery(id+"F0.wireOp",EDGE,"E75"),sQuery(id+"F0.wireOp",EDGE,"E76"),sQuery(id+"F0.wireOp",EDGE,"E77"),sQuery(id+"F0.wireOp",EDGE,"E78"),sQuery(id+"F0.wireOp",EDGE,"E79"),sQuery(id+"F0.wireOp",EDGE,"E80"),sQuery(id+"F0.wireOp",EDGE,"E81"),sQuery(id+"F0.wireOp",EDGE,"E82"),sQuery(id+"F0.wireOp",EDGE,"E83"),sQuery(id+"F0.wireOp",EDGE,"E84"),sQuery(id+"F0.wireOp",EDGE,"E85"),sQuery(id+"F0.wireOp",EDGE,"E86"),sQuery(id+"F0.wireOp",EDGE,"E87"),sQuery(id+"F0.wireOp",EDGE,"E88"),sQuery(id+"F0.wireOp",EDGE,"E89"),sQuery(id+"F0.wireOp",EDGE,"E90"),sQuery(id+"F0.wireOp",EDGE,"E91"),sQuery(id+"F0.wireOp",EDGE,"E92"),sQuery(id+"F0.wireOp",EDGE,"E93"),sQuery(id+"F0.wireOp",EDGE,"E94"),sQuery(id+"F0.wireOp",EDGE,"E95"),sQuery(id+"F0.wireOp",EDGE,"E96"),sQuery(id+"F0.wireOp",EDGE,"E97"),sQuery(id+"F0.wireOp",EDGE,"E98"),sQuery(id+"F0.wireOp",EDGE,"E99"),sQuery(id+"F0.wireOp",EDGE,"E100"),sQuery(id+"F0.wireOp",EDGE,"E101"),sQuery(id+"F0.wireOp",EDGE,"E102"),sQuery(id+"F0.wireOp",EDGE,"E103"),sQuery(id+"F0.wireOp",EDGE,"E104"),sQuery(id+"F0.wireOp",EDGE,"E105"),sQuery(id+"F0.wireOp",EDGE,"E106"),sQuery(id+"F0.wireOp",EDGE,"E107"),sQuery(id+"F0.wireOp",EDGE,"E108"),sQuery(id+"F0.wireOp",EDGE,"E109"),sQuery(id+"F0.wireOp",EDGE,"E110"),sQuery(id+"F0.wireOp",EDGE,"E111"),sQuery(id+"F0.wireOp",EDGE,"E112"),sQuery(id+"F0.wireOp",EDGE,"E113"),sQuery(id+"F0.wireOp",EDGE,"E114"),sQuery(id+"F0.wireOp",EDGE,"E115"),sQuery(id+"F0.wireOp",EDGE,"E116"),sQuery(id+"F0.wireOp",EDGE,"E117"),sQuery(id+"F0.wireOp",EDGE,"E118"),sQuery(id+"F0.wireOp",EDGE,"E119"),sQuery(id+"F0.wireOp",EDGE,"E120"),sQuery(id+"F0.wireOp",EDGE,"E121"),sQuery(id+"F0.wireOp",EDGE,"E122"),sQuery(id+"F0.wireOp",EDGE,"E123"),sQuery(id+"F0.wireOp",EDGE,"E124"),sQuery(id+"F0.wireOp",EDGE,"E125"),sQuery(id+"F0.wireOp",EDGE,"E126"),sQuery(id+"F0.wireOp",EDGE,"E127"),sQuery(id+"F0.wireOp",EDGE,"E128"),sQuery(id+"F0.wireOp",EDGE,"E129"),sQuery(id+"F0.wireOp",EDGE,"E130"),sQuery(id+"F0.wireOp",EDGE,"E131"),sQuery(id+"F0.wireOp",EDGE,"E132"),sQuery(id+"F0.wireOp",EDGE,"E133"),sQuery(id+"F0.wireOp",EDGE,"E134"),sQuery(id+"F0.wireOp",EDGE,"E135"),sQuery(id+"F0.wireOp",EDGE,"E136"),sQuery(id+"F0.wireOp",EDGE,"E137"),sQuery(id+"F0.wireOp",EDGE,"E138"),sQuery(id+"F0.wireOp",EDGE,"E139"),sQuery(id+"F0.wireOp",EDGE,"E140"),sQuery(id+"F0.wireOp",EDGE,"E141"),sQuery(id+"F0.wireOp",EDGE,"E142"),sQuery(id+"F0.wireOp",EDGE,"E143"),sQuery(id+"F0.wireOp",EDGE,"E144"),sQuery(id+"F0.wireOp",EDGE,"E145"),sQuery(id+"F0.wireOp",EDGE,"E146"),sQuery(id+"F0.wireOp",EDGE,"E147"),sQuery(id+"F0.wireOp",EDGE,"E148"),sQuery(id+"F0.wireOp",EDGE,"E149"),sQuery(id+"F0.wireOp",EDGE,"E150"),sQuery(id+"F0.wireOp",EDGE,"E151"),sQuery(id+"F0.wireOp",EDGE,"E152"),sQuery(id+"F0.wireOp",EDGE,"E153"),sQuery(id+"F0.wireOp",EDGE,"E154"),sQuery(id+"F0.wireOp",EDGE,"E155"),sQuery(id+"F0.wireOp",EDGE,"E156"),sQuery(id+"F0.wireOp",EDGE,"E157"),sQuery(id+"F0.wireOp",EDGE,"E158"),sQuery(id+"F0.wireOp",EDGE,"E159"),sQuery(id+"F0.wireOp",EDGE,"E160"),sQuery(id+"F0.wireOp",EDGE,"E161"),sQuery(id+"F0.wireOp",EDGE,"E162"),sQuery(id+"F0.wireOp",EDGE,"E163"),sQuery(id+"F0.wireOp",EDGE,"E164"),sQuery(id+"F0.wireOp",EDGE,"E165"),sQuery(id+"F0.wireOp",EDGE,"E166")])]});
            var Q5;
            Q5=makeQuery(id+"F1.opExtrude","SWEPT_BODY",BODY,{"disambiguationData":[OSD([sQuery(id+"F0.wireOp",EDGE,"E167"),sQuery(id+"F0.wireOp",EDGE,"E169"),sQuery(id+"F0.wireOp",EDGE,"E170"),sQuery(id+"F0.wireOp",EDGE,"E171"),sQuery(id+"F0.wireOp",EDGE,"E172"),sQuery(id+"F0.wireOp",EDGE,"E173"),sQuery(id+"F0.wireOp",EDGE,"E174"),sQuery(id+"F0.wireOp",EDGE,"E175"),sQuery(id+"F0.wireOp",EDGE,"E176"),sQuery(id+"F0.wireOp",EDGE,"E177"),sQuery(id+"F0.wireOp",EDGE,"E178"),sQuery(id+"F0.wireOp",EDGE,"E179"),sQuery(id+"F0.wireOp",EDGE,"E180"),sQuery(id+"F0.wireOp",EDGE,"E181"),sQuery(id+"F0.wireOp",EDGE,"E182"),sQuery(id+"F0.wireOp",EDGE,"E183"),sQuery(id+"F0.wireOp",EDGE,"E184"),sQuery(id+"F0.wireOp",EDGE,"E185"),sQuery(id+"F0.wireOp",EDGE,"E186"),sQuery(id+"F0.wireOp",EDGE,"E187"),sQuery(id+"F0.wireOp",EDGE,"E188"),sQuery(id+"F0.wireOp",EDGE,"E189"),sQuery(id+"F0.wireOp",EDGE,"E190"),sQuery(id+"F0.wireOp",EDGE,"E191"),sQuery(id+"F0.wireOp",EDGE,"E192"),sQuery(id+"F0.wireOp",EDGE,"E193"),sQuery(id+"F0.wireOp",EDGE,"E194"),sQuery(id+"F0.wireOp",EDGE,"E195"),sQuery(id+"F0.wireOp",EDGE,"E196"),sQuery(id+"F0.wireOp",EDGE,"E197"),sQuery(id+"F0.wireOp",EDGE,"E198"),sQuery(id+"F0.wireOp",EDGE,"E199"),sQuery(id+"F0.wireOp",EDGE,"E200"),sQuery(id+"F0.wireOp",EDGE,"E201"),sQuery(id+"F0.wireOp",EDGE,"E202"),sQuery(id+"F0.wireOp",EDGE,"E203"),sQuery(id+"F0.wireOp",EDGE,"E204"),sQuery(id+"F0.wireOp",EDGE,"E205"),sQuery(id+"F0.wireOp",EDGE,"E206"),sQuery(id+"F0.wireOp",EDGE,"E207"),sQuery(id+"F0.wireOp",EDGE,"E208"),sQuery(id+"F0.wireOp",EDGE,"E209"),sQuery(id+"F0.wireOp",EDGE,"E210"),sQuery(id+"F0.wireOp",EDGE,"E429"),sQuery(id+"F0.wireOp",EDGE,"E430"),sQuery(id+"F0.wireOp",EDGE,"E431"),sQuery(id+"F0.wireOp",EDGE,"E432"),sQuery(id+"F0.wireOp",EDGE,"E433"),sQuery(id+"F0.wireOp",EDGE,"E434"),sQuery(id+"F0.wireOp",EDGE,"E437"),sQuery(id+"F0.wireOp",EDGE,"E438"),sQuery(id+"F0.wireOp",EDGE,"E439"),sQuery(id+"F0.wireOp",EDGE,"E440"),sQuery(id+"F0.wireOp",EDGE,"E441"),sQuery(id+"F0.wireOp",EDGE,"E442"),sQuery(id+"F0.wireOp",EDGE,"E443"),sQuery(id+"F0.wireOp",EDGE,"E444"),sQuery(id+"F0.wireOp",EDGE,"E445"),sQuery(id+"F0.wireOp",EDGE,"E446"),sQuery(id+"F0.wireOp",EDGE,"E447"),sQuery(id+"F0.wireOp",EDGE,"E448"),sQuery(id+"F0.wireOp",EDGE,"E449"),sQuery(id+"F0.wireOp",EDGE,"E450"),sQuery(id+"F0.wireOp",EDGE,"E451"),sQuery(id+"F0.wireOp",EDGE,"E452"),sQuery(id+"F0.wireOp",EDGE,"E453"),sQuery(id+"F0.wireOp",EDGE,"E454"),sQuery(id+"F0.wireOp",EDGE,"E455"),sQuery(id+"F0.wireOp",EDGE,"E456"),sQuery(id+"F0.wireOp",EDGE,"E457"),sQuery(id+"F0.wireOp",EDGE,"E458"),sQuery(id+"F0.wireOp",EDGE,"E459"),sQuery(id+"F0.wireOp",EDGE,"E460"),sQuery(id+"F0.wireOp",EDGE,"E461"),sQuery(id+"F0.wireOp",EDGE,"E462"),sQuery(id+"F0.wireOp",EDGE,"E463"),sQuery(id+"F0.wireOp",EDGE,"E464"),sQuery(id+"F0.wireOp",EDGE,"E465"),sQuery(id+"F0.wireOp",EDGE,"E466")])]});
            var Q6;
            Q6=qCreatedBy(makeId("Origin.pointOp"),VERTEX);
            transform(context, id + "F10", {"entities" : qUnion([Q0, Q1, Q2, Q3, Q4, Q5]), "transformType" : TransformType.SCALE_UNIFORMLY, "scale" : .5, "scalePoint" : qUnion([Q6]), "makeCopy" : false});
        }
        {
            var Q0;
            Q0=makeQuery(id+"F5.opExtrude","CAP_FACE",FACE,{"disambiguationData":[OSD([sQuery(id+"F4.wireOp",EDGE,"E471.bottom"),sQuery(id+"F4.wireOp",EDGE,"E471.top"),sQuery(id+"F4.wireOp",EDGE,"E471.left"),sQuery(id+"F4.wireOp",EDGE,"E471.right"),sQuery(id+"F4.wireOp",EDGE,"E472.filletArc"),sQuery(id+"F4.wireOp",EDGE,"E473.filletArc"),sQuery(id+"F4.wireOp",EDGE,"E474.filletArc"),sQuery(id+"F4.wireOp",EDGE,"E475.filletArc")])],"isStart":false});
            var sketch = newSketch(context, id + "F11", { "sketchPlane" : qUnion([Q0])});
            skArc(sketch, "E482.0.0", {"start": v(37, 2) * mm, "mid": v(36.41, 3.41) * mm, "end": v(35, 4) * mm});
            skLineSegment(sketch, "E482.0.1", {"start": v(35, 4) * mm, "end": v(-23, 4) * mm});
            skArc(sketch, "E482.0.2", {"start": v(-23, 4) * mm, "mid": v(-24.41, 3.41) * mm, "end": v(-25, 2) * mm});
            skLineSegment(sketch, "E482.0.3", {"start": v(-25, 2) * mm, "end": v(-25, -2) * mm});
            skArc(sketch, "E482.0.4", {"start": v(-25, -2) * mm, "mid": v(-24.41, -3.41) * mm, "end": v(-23, -4) * mm});
            skLineSegment(sketch, "E482.0.5", {"start": v(-23, -4) * mm, "end": v(35, -4) * mm});
            skArc(sketch, "E482.0.6", {"start": v(35, -4) * mm, "mid": v(36.41, -3.41) * mm, "end": v(37, -2) * mm});
            skLineSegment(sketch, "E482.0.7", {"start": v(37, -2) * mm, "end": v(37, 2) * mm});
            skLineSegment(sketch, "E483.bottom", {"start": v(-22.91, 3.41) * mm, "end": v(34.91, 3.41) * mm});
            skLineSegment(sketch, "E483.top", {"start": v(-22.91, -3.41) * mm, "end": v(34.91, -3.41) * mm});
            skLineSegment(sketch, "E483.left", {"start": v(-24.41, 1.91) * mm, "end": v(-24.41, 1.32) * mm});
            skLineSegment(sketch, "E483.right", {"start": v(36.41, 1.91) * mm, "end": v(36.41, 1.32) * mm});
            skPoint(sketch, "E484.visualSharp", {"position": v(-24.41, 3.41) * mm});
            skArc(sketch, "E484.filletArc", {"start": v(-22.91, 3.41) * mm, "mid": v(-23.97, 2.97) * mm, "end": v(-24.41, 1.91) * mm});
            skPoint(sketch, "E485.visualSharp", {"position": v(-24.41, -3.41) * mm});
            skArc(sketch, "E485.filletArc", {"start": v(-24.41, -1.91) * mm, "mid": v(-23.97, -2.97) * mm, "end": v(-22.91, -3.41) * mm});
            skPoint(sketch, "E486.visualSharp", {"position": v(36.41, -3.41) * mm});
            skArc(sketch, "E486.filletArc", {"start": v(34.91, -3.41) * mm, "mid": v(35.97, -2.97) * mm, "end": v(36.41, -1.91) * mm});
            skPoint(sketch, "E487.visualSharp", {"position": v(36.41, 3.41) * mm});
            skArc(sketch, "E487.filletArc", {"start": v(36.41, 1.91) * mm, "mid": v(35.97, 2.97) * mm, "end": v(34.91, 3.41) * mm});
            skCircle(sketch, "E488", {"center": v(-22.91, 0) * mm, "radius": 1.45 * mm});
            skCircle(sketch, "E489", {"center": v(34.91, 0) * mm, "radius": 1.45 * mm});
            skArc(sketch, "E490", {"start": v(-24.41, -1.32) * mm, "mid": v(-20.91, 0) * mm, "end": v(-24.41, 1.32) * mm});
            skArc(sketch, "E491", {"start": v(36.41, 1.32) * mm, "mid": v(32.91, 0) * mm, "end": v(36.41, -1.32) * mm});
            skLineSegment(sketch, "E492.trimOffspring", {"start": v(-24.41, -1.32) * mm, "end": v(-24.41, -1.91) * mm});
            skLineSegment(sketch, "E493.trimOffspring", {"start": v(36.41, -1.32) * mm, "end": v(36.41, -1.91) * mm});
            skSolve(sketch);
        }
        {
            var Q0;
            Q0 = qSketchRegion(id + "F11", true);
            extrude(context, id + "F12", {"entities" : qUnion([Q0]), "depth" : 1 * mm, "offsetDistance" : 25 * mm});
        }
        {
            var Q0;
            Q0 = qSketchRegion(id + "F9", true);
            extrude(context, id + "F13", {"entities" : qUnion([Q0]), "operationType" : NewBodyOperationType.REMOVE, "depth" : 38.5 * mm, "offsetDistance" : 25 * mm, "hasSecondDirection" : true, "secondDirectionOppositeDirection" : true, "secondDirectionDepth" : 26.7 * mm});
        }
        {
            var Q0;
            Q0=qCreatedBy(makeId("Top.planeOp"),FACE);
            var sketch = newSketch(context, id + "F14", { "sketchPlane" : qUnion([Q0])});
            skCircle(sketch, "E494.0", {"center": v(-22.91, 0) * mm, "radius": 1.45 * mm});
            skCircle(sketch, "E495.0", {"center": v(34.91, 0) * mm, "radius": 1.45 * mm});
            skSolve(sketch);
        }
        {
            var Q0;
            Q0=makeQuery(id+"F14.imprint","IMPRINT",FACE,{"disambiguationData":[TD([[makeQuery(id+"F14.imprint","IMPRINT",EDGE,{"derivedFrom":sQuery(id+"F14.wireOp",EDGE,"E494.0")}),1.0]])]});
            var Q1;
            Q1=makeQuery(id+"F14.imprint","IMPRINT",FACE,{"disambiguationData":[TD([[makeQuery(id+"F14.imprint","IMPRINT",EDGE,{"derivedFrom":sQuery(id+"F14.wireOp",EDGE,"E495.0")}),1.0]])]});
            extrude(context, id + "F15", {"entities" : qUnion([Q0, Q1]), "operationType" : NewBodyOperationType.REMOVE, "oppositeDirection" : true, "depth" : 2 * mm, "offsetDistance" : 25 * mm, "hasSecondDirection" : true, "secondDirectionOppositeDirection" : false, "secondDirectionDepth" : 3 * mm});
        }
        {
            var Q0;
            Q0=makeQuery(id+"F13.boolean.opBoolean","COPY",FACE,{"derivedFrom":makeQuery(id+"F13.opExtrude","SWEPT_FACE",FACE,{"disambiguationData":[OSD([sQuery(id+"F9.wireOp",EDGE,"E478")])]})});
            fillet(context, id + "F16", {"entities" : qUnion([Q0]), "radius" : .2 * mm, "allowEdgeOverflow" : false});
        }
        {
            var Q0;
            Q0=makeQuery(id+"F5.opExtrude","CAP_FACE",FACE,{"disambiguationData":[OSD([sQuery(id+"F4.wireOp",EDGE,"E471.bottom"),sQuery(id+"F4.wireOp",EDGE,"E471.top"),sQuery(id+"F4.wireOp",EDGE,"E471.left"),sQuery(id+"F4.wireOp",EDGE,"E471.right"),sQuery(id+"F4.wireOp",EDGE,"E472.filletArc"),sQuery(id+"F4.wireOp",EDGE,"E473.filletArc"),sQuery(id+"F4.wireOp",EDGE,"E474.filletArc"),sQuery(id+"F4.wireOp",EDGE,"E475.filletArc")])],"isStart":true});
            fillet(context, id + "F17", {"entities" : qUnion([Q0]), "radius" : .2 * mm, "tangentPropagation" : true, "allowEdgeOverflow" : false});
        }
        {
            var Q0;
            Q0=makeQuery(id+"F1.opExtrude","SWEPT_BODY",BODY,{"disambiguationData":[OSD([sQuery(id+"F0.wireOp",EDGE,"E211"),sQuery(id+"F0.wireOp",EDGE,"E212"),sQuery(id+"F0.wireOp",EDGE,"E213"),sQuery(id+"F0.wireOp",EDGE,"E214"),sQuery(id+"F0.wireOp",EDGE,"E215"),sQuery(id+"F0.wireOp",EDGE,"E216"),sQuery(id+"F0.wireOp",EDGE,"E217"),sQuery(id+"F0.wireOp",EDGE,"E218"),sQuery(id+"F0.wireOp",EDGE,"E219"),sQuery(id+"F0.wireOp",EDGE,"E220"),sQuery(id+"F0.wireOp",EDGE,"E221"),sQuery(id+"F0.wireOp",EDGE,"E222"),sQuery(id+"F0.wireOp",EDGE,"E223"),sQuery(id+"F0.wireOp",EDGE,"E224"),sQuery(id+"F0.wireOp",EDGE,"E225"),sQuery(id+"F0.wireOp",EDGE,"E226"),sQuery(id+"F0.wireOp",EDGE,"E227"),sQuery(id+"F0.wireOp",EDGE,"E228"),sQuery(id+"F0.wireOp",EDGE,"E229"),sQuery(id+"F0.wireOp",EDGE,"E230"),sQuery(id+"F0.wireOp",EDGE,"E231"),sQuery(id+"F0.wireOp",EDGE,"E232"),sQuery(id+"F0.wireOp",EDGE,"E233"),sQuery(id+"F0.wireOp",EDGE,"E234"),sQuery(id+"F0.wireOp",EDGE,"E235"),sQuery(id+"F0.wireOp",EDGE,"E236"),sQuery(id+"F0.wireOp",EDGE,"E237"),sQuery(id+"F0.wireOp",EDGE,"E238"),sQuery(id+"F0.wireOp",EDGE,"E239"),sQuery(id+"F0.wireOp",EDGE,"E240"),sQuery(id+"F0.wireOp",EDGE,"E241"),sQuery(id+"F0.wireOp",EDGE,"E242"),sQuery(id+"F0.wireOp",EDGE,"E243"),sQuery(id+"F0.wireOp",EDGE,"E244"),sQuery(id+"F0.wireOp",EDGE,"E245"),sQuery(id+"F0.wireOp",EDGE,"E246"),sQuery(id+"F0.wireOp",EDGE,"E247"),sQuery(id+"F0.wireOp",EDGE,"E248"),sQuery(id+"F0.wireOp",EDGE,"E249"),sQuery(id+"F0.wireOp",EDGE,"E250"),sQuery(id+"F0.wireOp",EDGE,"E251"),sQuery(id+"F0.wireOp",EDGE,"E252"),sQuery(id+"F0.wireOp",EDGE,"E253"),sQuery(id+"F0.wireOp",EDGE,"E254"),sQuery(id+"F0.wireOp",EDGE,"E255"),sQuery(id+"F0.wireOp",EDGE,"E256"),sQuery(id+"F0.wireOp",EDGE,"E257"),sQuery(id+"F0.wireOp",EDGE,"E258")])]});
            var Q1;
            Q1=makeQuery(id+"F1.opExtrude","SWEPT_BODY",BODY,{"disambiguationData":[OSD([sQuery(id+"F0.wireOp",EDGE,"E259"),sQuery(id+"F0.wireOp",EDGE,"E260"),sQuery(id+"F0.wireOp",EDGE,"E261"),sQuery(id+"F0.wireOp",EDGE,"E262"),sQuery(id+"F0.wireOp",EDGE,"E263"),sQuery(id+"F0.wireOp",EDGE,"E264"),sQuery(id+"F0.wireOp",EDGE,"E265"),sQuery(id+"F0.wireOp",EDGE,"E266"),sQuery(id+"F0.wireOp",EDGE,"E267"),sQuery(id+"F0.wireOp",EDGE,"E268"),sQuery(id+"F0.wireOp",EDGE,"E269"),sQuery(id+"F0.wireOp",EDGE,"E270")])]});
            var Q2;
            Q2=makeQuery(id+"F1.opExtrude","SWEPT_BODY",BODY,{"disambiguationData":[OSD([sQuery(id+"F0.wireOp",EDGE,"E271"),sQuery(id+"F0.wireOp",EDGE,"E272"),sQuery(id+"F0.wireOp",EDGE,"E273"),sQuery(id+"F0.wireOp",EDGE,"E274"),sQuery(id+"F0.wireOp",EDGE,"E275"),sQuery(id+"F0.wireOp",EDGE,"E276"),sQuery(id+"F0.wireOp",EDGE,"E277"),sQuery(id+"F0.wireOp",EDGE,"E278"),sQuery(id+"F0.wireOp",EDGE,"E279"),sQuery(id+"F0.wireOp",EDGE,"E280"),sQuery(id+"F0.wireOp",EDGE,"E281"),sQuery(id+"F0.wireOp",EDGE,"E282"),sQuery(id+"F0.wireOp",EDGE,"E283"),sQuery(id+"F0.wireOp",EDGE,"E284"),sQuery(id+"F0.wireOp",EDGE,"E285"),sQuery(id+"F0.wireOp",EDGE,"E286"),sQuery(id+"F0.wireOp",EDGE,"E287"),sQuery(id+"F0.wireOp",EDGE,"E288"),sQuery(id+"F0.wireOp",EDGE,"E289"),sQuery(id+"F0.wireOp",EDGE,"E290"),sQuery(id+"F0.wireOp",EDGE,"E291"),sQuery(id+"F0.wireOp",EDGE,"E292"),sQuery(id+"F0.wireOp",EDGE,"E293"),sQuery(id+"F0.wireOp",EDGE,"E294"),sQuery(id+"F0.wireOp",EDGE,"E295"),sQuery(id+"F0.wireOp",EDGE,"E296"),sQuery(id+"F0.wireOp",EDGE,"E297"),sQuery(id+"F0.wireOp",EDGE,"E298"),sQuery(id+"F0.wireOp",EDGE,"E299"),sQuery(id+"F0.wireOp",EDGE,"E300"),sQuery(id+"F0.wireOp",EDGE,"E301"),sQuery(id+"F0.wireOp",EDGE,"E302"),sQuery(id+"F0.wireOp",EDGE,"E303"),sQuery(id+"F0.wireOp",EDGE,"E304"),sQuery(id+"F0.wireOp",EDGE,"E305"),sQuery(id+"F0.wireOp",EDGE,"E306"),sQuery(id+"F0.wireOp",EDGE,"E307"),sQuery(id+"F0.wireOp",EDGE,"E308"),sQuery(id+"F0.wireOp",EDGE,"E309"),sQuery(id+"F0.wireOp",EDGE,"E310"),sQuery(id+"F0.wireOp",EDGE,"E311")])]});
            var Q3;
            Q3=makeQuery(id+"F1.opExtrude","SWEPT_BODY",BODY,{"disambiguationData":[OSD([sQuery(id+"F0.wireOp",EDGE,"E312"),sQuery(id+"F0.wireOp",EDGE,"E313"),sQuery(id+"F0.wireOp",EDGE,"E314"),sQuery(id+"F0.wireOp",EDGE,"E315"),sQuery(id+"F0.wireOp",EDGE,"E316"),sQuery(id+"F0.wireOp",EDGE,"E317"),sQuery(id+"F0.wireOp",EDGE,"E318"),sQuery(id+"F0.wireOp",EDGE,"E319"),sQuery(id+"F0.wireOp",EDGE,"E320"),sQuery(id+"F0.wireOp",EDGE,"E321"),sQuery(id+"F0.wireOp",EDGE,"E322"),sQuery(id+"F0.wireOp",EDGE,"E323"),sQuery(id+"F0.wireOp",EDGE,"E324"),sQuery(id+"F0.wireOp",EDGE,"E325"),sQuery(id+"F0.wireOp",EDGE,"E326"),sQuery(id+"F0.wireOp",EDGE,"E327"),sQuery(id+"F0.wireOp",EDGE,"E328"),sQuery(id+"F0.wireOp",EDGE,"E329"),sQuery(id+"F0.wireOp",EDGE,"E330"),sQuery(id+"F0.wireOp",EDGE,"E331"),sQuery(id+"F0.wireOp",EDGE,"E332"),sQuery(id+"F0.wireOp",EDGE,"E333"),sQuery(id+"F0.wireOp",EDGE,"E334"),sQuery(id+"F0.wireOp",EDGE,"E335"),sQuery(id+"F0.wireOp",EDGE,"E336"),sQuery(id+"F0.wireOp",EDGE,"E337"),sQuery(id+"F0.wireOp",EDGE,"E338"),sQuery(id+"F0.wireOp",EDGE,"E339"),sQuery(id+"F0.wireOp",EDGE,"E340"),sQuery(id+"F0.wireOp",EDGE,"E341"),sQuery(id+"F0.wireOp",EDGE,"E342"),sQuery(id+"F0.wireOp",EDGE,"E343"),sQuery(id+"F0.wireOp",EDGE,"E344"),sQuery(id+"F0.wireOp",EDGE,"E345"),sQuery(id+"F0.wireOp",EDGE,"E346"),sQuery(id+"F0.wireOp",EDGE,"E347"),sQuery(id+"F0.wireOp",EDGE,"E348"),sQuery(id+"F0.wireOp",EDGE,"E349"),sQuery(id+"F0.wireOp",EDGE,"E350"),sQuery(id+"F0.wireOp",EDGE,"E351"),sQuery(id+"F0.wireOp",EDGE,"E352"),sQuery(id+"F0.wireOp",EDGE,"E353"),sQuery(id+"F0.wireOp",EDGE,"E354"),sQuery(id+"F0.wireOp",EDGE,"E355"),sQuery(id+"F0.wireOp",EDGE,"E356"),sQuery(id+"F0.wireOp",EDGE,"E357"),sQuery(id+"F0.wireOp",EDGE,"E358"),sQuery(id+"F0.wireOp",EDGE,"E359"),sQuery(id+"F0.wireOp",EDGE,"E360"),sQuery(id+"F0.wireOp",EDGE,"E361"),sQuery(id+"F0.wireOp",EDGE,"E362"),sQuery(id+"F0.wireOp",EDGE,"E363"),sQuery(id+"F0.wireOp",EDGE,"E364"),sQuery(id+"F0.wireOp",EDGE,"E365"),sQuery(id+"F0.wireOp",EDGE,"E366"),sQuery(id+"F0.wireOp",EDGE,"E367"),sQuery(id+"F0.wireOp",EDGE,"E368"),sQuery(id+"F0.wireOp",EDGE,"E369"),sQuery(id+"F0.wireOp",EDGE,"E370"),sQuery(id+"F0.wireOp",EDGE,"E371"),sQuery(id+"F0.wireOp",EDGE,"E372"),sQuery(id+"F0.wireOp",EDGE,"E373"),sQuery(id+"F0.wireOp",EDGE,"E374"),sQuery(id+"F0.wireOp",EDGE,"E375"),sQuery(id+"F0.wireOp",EDGE,"E376"),sQuery(id+"F0.wireOp",EDGE,"E377"),sQuery(id+"F0.wireOp",EDGE,"E378"),sQuery(id+"F0.wireOp",EDGE,"E379"),sQuery(id+"F0.wireOp",EDGE,"E380"),sQuery(id+"F0.wireOp",EDGE,"E381"),sQuery(id+"F0.wireOp",EDGE,"E382"),sQuery(id+"F0.wireOp",EDGE,"E383"),sQuery(id+"F0.wireOp",EDGE,"E384"),sQuery(id+"F0.wireOp",EDGE,"E385"),sQuery(id+"F0.wireOp",EDGE,"E386"),sQuery(id+"F0.wireOp",EDGE,"E387"),sQuery(id+"F0.wireOp",EDGE,"E388"),sQuery(id+"F0.wireOp",EDGE,"E389"),sQuery(id+"F0.wireOp",EDGE,"E390"),sQuery(id+"F0.wireOp",EDGE,"E391"),sQuery(id+"F0.wireOp",EDGE,"E392"),sQuery(id+"F0.wireOp",EDGE,"E393"),sQuery(id+"F0.wireOp",EDGE,"E394"),sQuery(id+"F0.wireOp",EDGE,"E395"),sQuery(id+"F0.wireOp",EDGE,"E396"),sQuery(id+"F0.wireOp",EDGE,"E397"),sQuery(id+"F0.wireOp",EDGE,"E398"),sQuery(id+"F0.wireOp",EDGE,"E399"),sQuery(id+"F0.wireOp",EDGE,"E400"),sQuery(id+"F0.wireOp",EDGE,"E401"),sQuery(id+"F0.wireOp",EDGE,"E402"),sQuery(id+"F0.wireOp",EDGE,"E403"),sQuery(id+"F0.wireOp",EDGE,"E404"),sQuery(id+"F0.wireOp",EDGE,"E405"),sQuery(id+"F0.wireOp",EDGE,"E406"),sQuery(id+"F0.wireOp",EDGE,"E407"),sQuery(id+"F0.wireOp",EDGE,"E408"),sQuery(id+"F0.wireOp",EDGE,"E409"),sQuery(id+"F0.wireOp",EDGE,"E410"),sQuery(id+"F0.wireOp",EDGE,"E411"),sQuery(id+"F0.wireOp",EDGE,"E412"),sQuery(id+"F0.wireOp",EDGE,"E413"),sQuery(id+"F0.wireOp",EDGE,"E414"),sQuery(id+"F0.wireOp",EDGE,"E415"),sQuery(id+"F0.wireOp",EDGE,"E416"),sQuery(id+"F0.wireOp",EDGE,"E417"),sQuery(id+"F0.wireOp",EDGE,"E418"),sQuery(id+"F0.wireOp",EDGE,"E419"),sQuery(id+"F0.wireOp",EDGE,"E420"),sQuery(id+"F0.wireOp",EDGE,"E421"),sQuery(id+"F0.wireOp",EDGE,"E422"),sQuery(id+"F0.wireOp",EDGE,"E423"),sQuery(id+"F0.wireOp",EDGE,"E424"),sQuery(id+"F0.wireOp",EDGE,"E425"),sQuery(id+"F0.wireOp",EDGE,"E426"),sQuery(id+"F0.wireOp",EDGE,"E427"),sQuery(id+"F0.wireOp",EDGE,"E428")])]});
            var Q4;
            Q4=makeQuery(id+"F5.opExtrude","SWEPT_BODY",BODY,{"disambiguationData":[OSD([sQuery(id+"F4.wireOp",EDGE,"E471.bottom"),sQuery(id+"F4.wireOp",EDGE,"E471.top"),sQuery(id+"F4.wireOp",EDGE,"E471.left"),sQuery(id+"F4.wireOp",EDGE,"E471.right"),sQuery(id+"F4.wireOp",EDGE,"E472.filletArc"),sQuery(id+"F4.wireOp",EDGE,"E473.filletArc"),sQuery(id+"F4.wireOp",EDGE,"E474.filletArc"),sQuery(id+"F4.wireOp",EDGE,"E475.filletArc")])]});
            var Q5;
            Q5=makeQuery(id+"F12.opExtrude","SWEPT_BODY",BODY,{"disambiguationData":[OSD([sQuery(id+"F11.wireOp",EDGE,"E482.0.0"),sQuery(id+"F11.wireOp",EDGE,"E482.0.1"),sQuery(id+"F11.wireOp",EDGE,"E482.0.2"),sQuery(id+"F11.wireOp",EDGE,"E482.0.3"),sQuery(id+"F11.wireOp",EDGE,"E482.0.4"),sQuery(id+"F11.wireOp",EDGE,"E482.0.5"),sQuery(id+"F11.wireOp",EDGE,"E482.0.6"),sQuery(id+"F11.wireOp",EDGE,"E482.0.7"),sQuery(id+"F11.wireOp",EDGE,"E483.bottom"),sQuery(id+"F11.wireOp",EDGE,"E483.top"),sQuery(id+"F11.wireOp",EDGE,"E483.left"),sQuery(id+"F11.wireOp",EDGE,"E483.right"),sQuery(id+"F11.wireOp",EDGE,"E484.filletArc"),sQuery(id+"F11.wireOp",EDGE,"E485.filletArc"),sQuery(id+"F11.wireOp",EDGE,"E486.filletArc"),sQuery(id+"F11.wireOp",EDGE,"E487.filletArc"),sQuery(id+"F11.wireOp",EDGE,"E488"),sQuery(id+"F11.wireOp",EDGE,"E489"),sQuery(id+"F11.wireOp",EDGE,"E490"),sQuery(id+"F11.wireOp",EDGE,"E491"),sQuery(id+"F11.wireOp",EDGE,"E492.trimOffspring"),sQuery(id+"F11.wireOp",EDGE,"E493.trimOffspring")])]});
            var Q6;
            Q6=makeQuery(id+"F1.opExtrude","SWEPT_BODY",BODY,{"disambiguationData":[OSD([sQuery(id+"F0.wireOp",EDGE,"E167"),sQuery(id+"F0.wireOp",EDGE,"E169"),sQuery(id+"F0.wireOp",EDGE,"E170"),sQuery(id+"F0.wireOp",EDGE,"E171"),sQuery(id+"F0.wireOp",EDGE,"E172"),sQuery(id+"F0.wireOp",EDGE,"E173"),sQuery(id+"F0.wireOp",EDGE,"E174"),sQuery(id+"F0.wireOp",EDGE,"E175"),sQuery(id+"F0.wireOp",EDGE,"E176"),sQuery(id+"F0.wireOp",EDGE,"E177"),sQuery(id+"F0.wireOp",EDGE,"E178"),sQuery(id+"F0.wireOp",EDGE,"E179"),sQuery(id+"F0.wireOp",EDGE,"E180"),sQuery(id+"F0.wireOp",EDGE,"E181"),sQuery(id+"F0.wireOp",EDGE,"E182"),sQuery(id+"F0.wireOp",EDGE,"E183"),sQuery(id+"F0.wireOp",EDGE,"E184"),sQuery(id+"F0.wireOp",EDGE,"E185"),sQuery(id+"F0.wireOp",EDGE,"E186"),sQuery(id+"F0.wireOp",EDGE,"E187"),sQuery(id+"F0.wireOp",EDGE,"E188"),sQuery(id+"F0.wireOp",EDGE,"E189"),sQuery(id+"F0.wireOp",EDGE,"E190"),sQuery(id+"F0.wireOp",EDGE,"E191"),sQuery(id+"F0.wireOp",EDGE,"E192"),sQuery(id+"F0.wireOp",EDGE,"E193"),sQuery(id+"F0.wireOp",EDGE,"E194"),sQuery(id+"F0.wireOp",EDGE,"E195"),sQuery(id+"F0.wireOp",EDGE,"E196"),sQuery(id+"F0.wireOp",EDGE,"E197"),sQuery(id+"F0.wireOp",EDGE,"E198"),sQuery(id+"F0.wireOp",EDGE,"E199"),sQuery(id+"F0.wireOp",EDGE,"E200"),sQuery(id+"F0.wireOp",EDGE,"E201"),sQuery(id+"F0.wireOp",EDGE,"E202"),sQuery(id+"F0.wireOp",EDGE,"E203"),sQuery(id+"F0.wireOp",EDGE,"E204"),sQuery(id+"F0.wireOp",EDGE,"E205"),sQuery(id+"F0.wireOp",EDGE,"E206"),sQuery(id+"F0.wireOp",EDGE,"E207"),sQuery(id+"F0.wireOp",EDGE,"E208"),sQuery(id+"F0.wireOp",EDGE,"E209"),sQuery(id+"F0.wireOp",EDGE,"E210"),sQuery(id+"F0.wireOp",EDGE,"E429"),sQuery(id+"F0.wireOp",EDGE,"E430"),sQuery(id+"F0.wireOp",EDGE,"E431"),sQuery(id+"F0.wireOp",EDGE,"E432"),sQuery(id+"F0.wireOp",EDGE,"E433"),sQuery(id+"F0.wireOp",EDGE,"E434"),sQuery(id+"F0.wireOp",EDGE,"E437"),sQuery(id+"F0.wireOp",EDGE,"E438"),sQuery(id+"F0.wireOp",EDGE,"E439"),sQuery(id+"F0.wireOp",EDGE,"E440"),sQuery(id+"F0.wireOp",EDGE,"E441"),sQuery(id+"F0.wireOp",EDGE,"E442"),sQuery(id+"F0.wireOp",EDGE,"E443"),sQuery(id+"F0.wireOp",EDGE,"E444"),sQuery(id+"F0.wireOp",EDGE,"E445"),sQuery(id+"F0.wireOp",EDGE,"E446"),sQuery(id+"F0.wireOp",EDGE,"E447"),sQuery(id+"F0.wireOp",EDGE,"E448"),sQuery(id+"F0.wireOp",EDGE,"E449"),sQuery(id+"F0.wireOp",EDGE,"E450"),sQuery(id+"F0.wireOp",EDGE,"E451"),sQuery(id+"F0.wireOp",EDGE,"E452"),sQuery(id+"F0.wireOp",EDGE,"E453"),sQuery(id+"F0.wireOp",EDGE,"E454"),sQuery(id+"F0.wireOp",EDGE,"E455"),sQuery(id+"F0.wireOp",EDGE,"E456"),sQuery(id+"F0.wireOp",EDGE,"E457"),sQuery(id+"F0.wireOp",EDGE,"E458"),sQuery(id+"F0.wireOp",EDGE,"E459"),sQuery(id+"F0.wireOp",EDGE,"E460"),sQuery(id+"F0.wireOp",EDGE,"E461"),sQuery(id+"F0.wireOp",EDGE,"E462"),sQuery(id+"F0.wireOp",EDGE,"E463"),sQuery(id+"F0.wireOp",EDGE,"E464"),sQuery(id+"F0.wireOp",EDGE,"E465"),sQuery(id+"F0.wireOp",EDGE,"E466")])]});
            var Q7;
            Q7=makeQuery(id+"F1.opExtrude","SWEPT_BODY",BODY,{"disambiguationData":[OSD([sQuery(id+"F0.wireOp",EDGE,"E0"),sQuery(id+"F0.wireOp",EDGE,"E1"),sQuery(id+"F0.wireOp",EDGE,"E2"),sQuery(id+"F0.wireOp",EDGE,"E3"),sQuery(id+"F0.wireOp",EDGE,"E4"),sQuery(id+"F0.wireOp",EDGE,"E5"),sQuery(id+"F0.wireOp",EDGE,"E6"),sQuery(id+"F0.wireOp",EDGE,"E7"),sQuery(id+"F0.wireOp",EDGE,"E8"),sQuery(id+"F0.wireOp",EDGE,"E9"),sQuery(id+"F0.wireOp",EDGE,"E10"),sQuery(id+"F0.wireOp",EDGE,"E11"),sQuery(id+"F0.wireOp",EDGE,"E12"),sQuery(id+"F0.wireOp",EDGE,"E13"),sQuery(id+"F0.wireOp",EDGE,"E14"),sQuery(id+"F0.wireOp",EDGE,"E15"),sQuery(id+"F0.wireOp",EDGE,"E16"),sQuery(id+"F0.wireOp",EDGE,"E17"),sQuery(id+"F0.wireOp",EDGE,"E18"),sQuery(id+"F0.wireOp",EDGE,"E19"),sQuery(id+"F0.wireOp",EDGE,"E20"),sQuery(id+"F0.wireOp",EDGE,"E21"),sQuery(id+"F0.wireOp",EDGE,"E22"),sQuery(id+"F0.wireOp",EDGE,"E23"),sQuery(id+"F0.wireOp",EDGE,"E24"),sQuery(id+"F0.wireOp",EDGE,"E25"),sQuery(id+"F0.wireOp",EDGE,"E26"),sQuery(id+"F0.wireOp",EDGE,"E27"),sQuery(id+"F0.wireOp",EDGE,"E28"),sQuery(id+"F0.wireOp",EDGE,"E29"),sQuery(id+"F0.wireOp",EDGE,"E30"),sQuery(id+"F0.wireOp",EDGE,"E31"),sQuery(id+"F0.wireOp",EDGE,"E32"),sQuery(id+"F0.wireOp",EDGE,"E33"),sQuery(id+"F0.wireOp",EDGE,"E34"),sQuery(id+"F0.wireOp",EDGE,"E35"),sQuery(id+"F0.wireOp",EDGE,"E36"),sQuery(id+"F0.wireOp",EDGE,"E37"),sQuery(id+"F0.wireOp",EDGE,"E38"),sQuery(id+"F0.wireOp",EDGE,"E39"),sQuery(id+"F0.wireOp",EDGE,"E40"),sQuery(id+"F0.wireOp",EDGE,"E41"),sQuery(id+"F0.wireOp",EDGE,"E42"),sQuery(id+"F0.wireOp",EDGE,"E43"),sQuery(id+"F0.wireOp",EDGE,"E44"),sQuery(id+"F0.wireOp",EDGE,"E45"),sQuery(id+"F0.wireOp",EDGE,"E46"),sQuery(id+"F0.wireOp",EDGE,"E47"),sQuery(id+"F0.wireOp",EDGE,"E48"),sQuery(id+"F0.wireOp",EDGE,"E49"),sQuery(id+"F0.wireOp",EDGE,"E50"),sQuery(id+"F0.wireOp",EDGE,"E51"),sQuery(id+"F0.wireOp",EDGE,"E52"),sQuery(id+"F0.wireOp",EDGE,"E53"),sQuery(id+"F0.wireOp",EDGE,"E54"),sQuery(id+"F0.wireOp",EDGE,"E55"),sQuery(id+"F0.wireOp",EDGE,"E56"),sQuery(id+"F0.wireOp",EDGE,"E57"),sQuery(id+"F0.wireOp",EDGE,"E58"),sQuery(id+"F0.wireOp",EDGE,"E59"),sQuery(id+"F0.wireOp",EDGE,"E60"),sQuery(id+"F0.wireOp",EDGE,"E61"),sQuery(id+"F0.wireOp",EDGE,"E62"),sQuery(id+"F0.wireOp",EDGE,"E63"),sQuery(id+"F0.wireOp",EDGE,"E64"),sQuery(id+"F0.wireOp",EDGE,"E65"),sQuery(id+"F0.wireOp",EDGE,"E66"),sQuery(id+"F0.wireOp",EDGE,"E67"),sQuery(id+"F0.wireOp",EDGE,"E68"),sQuery(id+"F0.wireOp",EDGE,"E69"),sQuery(id+"F0.wireOp",EDGE,"E70"),sQuery(id+"F0.wireOp",EDGE,"E71"),sQuery(id+"F0.wireOp",EDGE,"E72"),sQuery(id+"F0.wireOp",EDGE,"E73"),sQuery(id+"F0.wireOp",EDGE,"E74"),sQuery(id+"F0.wireOp",EDGE,"E75"),sQuery(id+"F0.wireOp",EDGE,"E76"),sQuery(id+"F0.wireOp",EDGE,"E77"),sQuery(id+"F0.wireOp",EDGE,"E78"),sQuery(id+"F0.wireOp",EDGE,"E79"),sQuery(id+"F0.wireOp",EDGE,"E80"),sQuery(id+"F0.wireOp",EDGE,"E81"),sQuery(id+"F0.wireOp",EDGE,"E82"),sQuery(id+"F0.wireOp",EDGE,"E83"),sQuery(id+"F0.wireOp",EDGE,"E84"),sQuery(id+"F0.wireOp",EDGE,"E85"),sQuery(id+"F0.wireOp",EDGE,"E86"),sQuery(id+"F0.wireOp",EDGE,"E87"),sQuery(id+"F0.wireOp",EDGE,"E88"),sQuery(id+"F0.wireOp",EDGE,"E89"),sQuery(id+"F0.wireOp",EDGE,"E90"),sQuery(id+"F0.wireOp",EDGE,"E91"),sQuery(id+"F0.wireOp",EDGE,"E92"),sQuery(id+"F0.wireOp",EDGE,"E93"),sQuery(id+"F0.wireOp",EDGE,"E94"),sQuery(id+"F0.wireOp",EDGE,"E95"),sQuery(id+"F0.wireOp",EDGE,"E96"),sQuery(id+"F0.wireOp",EDGE,"E97"),sQuery(id+"F0.wireOp",EDGE,"E98"),sQuery(id+"F0.wireOp",EDGE,"E99"),sQuery(id+"F0.wireOp",EDGE,"E100"),sQuery(id+"F0.wireOp",EDGE,"E101"),sQuery(id+"F0.wireOp",EDGE,"E102"),sQuery(id+"F0.wireOp",EDGE,"E103"),sQuery(id+"F0.wireOp",EDGE,"E104"),sQuery(id+"F0.wireOp",EDGE,"E105"),sQuery(id+"F0.wireOp",EDGE,"E106"),sQuery(id+"F0.wireOp",EDGE,"E107"),sQuery(id+"F0.wireOp",EDGE,"E108"),sQuery(id+"F0.wireOp",EDGE,"E109"),sQuery(id+"F0.wireOp",EDGE,"E110"),sQuery(id+"F0.wireOp",EDGE,"E111"),sQuery(id+"F0.wireOp",EDGE,"E112"),sQuery(id+"F0.wireOp",EDGE,"E113"),sQuery(id+"F0.wireOp",EDGE,"E114"),sQuery(id+"F0.wireOp",EDGE,"E115"),sQuery(id+"F0.wireOp",EDGE,"E116"),sQuery(id+"F0.wireOp",EDGE,"E117"),sQuery(id+"F0.wireOp",EDGE,"E118"),sQuery(id+"F0.wireOp",EDGE,"E119"),sQuery(id+"F0.wireOp",EDGE,"E120"),sQuery(id+"F0.wireOp",EDGE,"E121"),sQuery(id+"F0.wireOp",EDGE,"E122"),sQuery(id+"F0.wireOp",EDGE,"E123"),sQuery(id+"F0.wireOp",EDGE,"E124"),sQuery(id+"F0.wireOp",EDGE,"E125"),sQuery(id+"F0.wireOp",EDGE,"E126"),sQuery(id+"F0.wireOp",EDGE,"E127"),sQuery(id+"F0.wireOp",EDGE,"E128"),sQuery(id+"F0.wireOp",EDGE,"E129"),sQuery(id+"F0.wireOp",EDGE,"E130"),sQuery(id+"F0.wireOp",EDGE,"E131"),sQuery(id+"F0.wireOp",EDGE,"E132"),sQuery(id+"F0.wireOp",EDGE,"E133"),sQuery(id+"F0.wireOp",EDGE,"E134"),sQuery(id+"F0.wireOp",EDGE,"E135"),sQuery(id+"F0.wireOp",EDGE,"E136"),sQuery(id+"F0.wireOp",EDGE,"E137"),sQuery(id+"F0.wireOp",EDGE,"E138"),sQuery(id+"F0.wireOp",EDGE,"E139"),sQuery(id+"F0.wireOp",EDGE,"E140"),sQuery(id+"F0.wireOp",EDGE,"E141"),sQuery(id+"F0.wireOp",EDGE,"E142"),sQuery(id+"F0.wireOp",EDGE,"E143"),sQuery(id+"F0.wireOp",EDGE,"E144"),sQuery(id+"F0.wireOp",EDGE,"E145"),sQuery(id+"F0.wireOp",EDGE,"E146"),sQuery(id+"F0.wireOp",EDGE,"E147"),sQuery(id+"F0.wireOp",EDGE,"E148"),sQuery(id+"F0.wireOp",EDGE,"E149"),sQuery(id+"F0.wireOp",EDGE,"E150"),sQuery(id+"F0.wireOp",EDGE,"E151"),sQuery(id+"F0.wireOp",EDGE,"E152"),sQuery(id+"F0.wireOp",EDGE,"E153"),sQuery(id+"F0.wireOp",EDGE,"E154"),sQuery(id+"F0.wireOp",EDGE,"E155"),sQuery(id+"F0.wireOp",EDGE,"E156"),sQuery(id+"F0.wireOp",EDGE,"E157"),sQuery(id+"F0.wireOp",EDGE,"E158"),sQuery(id+"F0.wireOp",EDGE,"E159"),sQuery(id+"F0.wireOp",EDGE,"E160"),sQuery(id+"F0.wireOp",EDGE,"E161"),sQuery(id+"F0.wireOp",EDGE,"E162"),sQuery(id+"F0.wireOp",EDGE,"E163"),sQuery(id+"F0.wireOp",EDGE,"E164"),sQuery(id+"F0.wireOp",EDGE,"E165"),sQuery(id+"F0.wireOp",EDGE,"E166")])]});
            var Q8;
            Q8=makeQuery(id+"F3.opExtrude","SWEPT_BODY",BODY,{"disambiguationData":[OSD([sQuery(id+"F2.wireOp",EDGE,"E467"),sQuery(id+"F2.wireOp",EDGE,"E468"),sQuery(id+"F2.wireOp",EDGE,"E469"),sQuery(id+"F2.wireOp",EDGE,"E470")])]});
            booleanBodies(context, id + "F18", {"operationType" : BooleanOperationType.UNION, "tools" : qUnion([Q0, Q1, Q2, Q3, Q4, Q5, Q6, Q7, Q8])});
        }
        {
            var Q0;
            {var subQ0=sQuery(id+"F2.wireOp",EDGE,"E468");var subQ1=makeQuery(id+"F3.opExtrude","CAP_FACE",FACE,{"disambiguationData":[OSD([sQuery(id+"F2.wireOp",EDGE,"E467"),subQ0,sQuery(id+"F2.wireOp",EDGE,"E469"),sQuery(id+"F2.wireOp",EDGE,"E470")])],"isStart":false});var subQ2=sQuery(id+"F4.wireOp",EDGE,"E475.filletArc");var subQ3=sQuery(id+"F4.wireOp",EDGE,"E474.filletArc");var subQ4=sQuery(id+"F4.wireOp",EDGE,"E473.filletArc");var subQ5=sQuery(id+"F4.wireOp",EDGE,"E472.filletArc");var subQ6=sQuery(id+"F4.wireOp",EDGE,"E471.right");var subQ7=sQuery(id+"F4.wireOp",EDGE,"E471.left");var subQ8=sQuery(id+"F4.wireOp",EDGE,"E471.top");var subQ9=sQuery(id+"F4.wireOp",EDGE,"E471.bottom");var subQ10=makeQuery(id+"F5.opExtrude","CAP_FACE",FACE,{"disambiguationData":[OSD([subQ9,subQ8,subQ7,subQ6,subQ5,subQ4,subQ3,subQ2])],"isStart":false});Q0=makeQuery(id+"F15.boolean.opBoolean","SPLIT",EDGE,{"disambiguationData":[TD([makeQuery(id+"F7.opFillet","BLEND_FACE",FACE,{"disambiguationData":[OSD([subQ0,subQ9,subQ8,subQ7,subQ6,subQ5,subQ4,subQ3,subQ2])]})])],"derivedFrom":makeQuery(id+"F6.opBoolean","INTERSECT",EDGE,{"derivedFrom":[subQ1,subQ10]})});}
            var Q1;
            {var subQ0=sQuery(id+"F2.wireOp",EDGE,"E469");var subQ1=makeQuery(id+"F3.opExtrude","CAP_FACE",FACE,{"disambiguationData":[OSD([sQuery(id+"F2.wireOp",EDGE,"E467"),sQuery(id+"F2.wireOp",EDGE,"E468"),subQ0,sQuery(id+"F2.wireOp",EDGE,"E470")])],"isStart":false});var subQ2=sQuery(id+"F4.wireOp",EDGE,"E475.filletArc");var subQ3=sQuery(id+"F4.wireOp",EDGE,"E474.filletArc");var subQ4=sQuery(id+"F4.wireOp",EDGE,"E473.filletArc");var subQ5=sQuery(id+"F4.wireOp",EDGE,"E472.filletArc");var subQ6=sQuery(id+"F4.wireOp",EDGE,"E471.right");var subQ7=sQuery(id+"F4.wireOp",EDGE,"E471.left");var subQ8=sQuery(id+"F4.wireOp",EDGE,"E471.top");var subQ9=sQuery(id+"F4.wireOp",EDGE,"E471.bottom");var subQ10=makeQuery(id+"F5.opExtrude","CAP_FACE",FACE,{"disambiguationData":[OSD([subQ9,subQ8,subQ7,subQ6,subQ5,subQ4,subQ3,subQ2])],"isStart":false});Q1=makeQuery(id+"F15.boolean.opBoolean","SPLIT",EDGE,{"disambiguationData":[TD([makeQuery(id+"F7.opFillet","BLEND_FACE",FACE,{"disambiguationData":[OSD([subQ0,subQ9,subQ8,subQ7,subQ6,subQ5,subQ4,subQ3,subQ2])]})])],"derivedFrom":makeQuery(id+"F6.opBoolean","INTERSECT",EDGE,{"derivedFrom":[subQ1,subQ10]})});}
            var Q2;
            {var subQ0=sQuery(id+"F2.wireOp",EDGE,"E469");var subQ1=makeQuery(id+"F3.opExtrude","CAP_FACE",FACE,{"disambiguationData":[OSD([sQuery(id+"F2.wireOp",EDGE,"E467"),sQuery(id+"F2.wireOp",EDGE,"E468"),subQ0,sQuery(id+"F2.wireOp",EDGE,"E470")])],"isStart":true});var subQ2=sQuery(id+"F4.wireOp",EDGE,"E475.filletArc");var subQ3=sQuery(id+"F4.wireOp",EDGE,"E474.filletArc");var subQ4=sQuery(id+"F4.wireOp",EDGE,"E473.filletArc");var subQ5=sQuery(id+"F4.wireOp",EDGE,"E472.filletArc");var subQ6=sQuery(id+"F4.wireOp",EDGE,"E471.right");var subQ7=sQuery(id+"F4.wireOp",EDGE,"E471.left");var subQ8=sQuery(id+"F4.wireOp",EDGE,"E471.top");var subQ9=sQuery(id+"F4.wireOp",EDGE,"E471.bottom");var subQ10=makeQuery(id+"F5.opExtrude","CAP_FACE",FACE,{"disambiguationData":[OSD([subQ9,subQ8,subQ7,subQ6,subQ5,subQ4,subQ3,subQ2])],"isStart":false});Q2=makeQuery(id+"F15.boolean.opBoolean","SPLIT",EDGE,{"disambiguationData":[TD([makeQuery(id+"F7.opFillet","BLEND_FACE",FACE,{"disambiguationData":[OSD([subQ0,subQ9,subQ8,subQ7,subQ6,subQ5,subQ4,subQ3,subQ2])]})])],"derivedFrom":makeQuery(id+"F6.opBoolean","INTERSECT",EDGE,{"derivedFrom":[subQ1,subQ10]})});}
            var Q3;
            {var subQ0=sQuery(id+"F2.wireOp",EDGE,"E468");var subQ1=makeQuery(id+"F3.opExtrude","CAP_FACE",FACE,{"disambiguationData":[OSD([sQuery(id+"F2.wireOp",EDGE,"E467"),subQ0,sQuery(id+"F2.wireOp",EDGE,"E469"),sQuery(id+"F2.wireOp",EDGE,"E470")])],"isStart":true});var subQ2=sQuery(id+"F4.wireOp",EDGE,"E475.filletArc");var subQ3=sQuery(id+"F4.wireOp",EDGE,"E474.filletArc");var subQ4=sQuery(id+"F4.wireOp",EDGE,"E473.filletArc");var subQ5=sQuery(id+"F4.wireOp",EDGE,"E472.filletArc");var subQ6=sQuery(id+"F4.wireOp",EDGE,"E471.right");var subQ7=sQuery(id+"F4.wireOp",EDGE,"E471.left");var subQ8=sQuery(id+"F4.wireOp",EDGE,"E471.top");var subQ9=sQuery(id+"F4.wireOp",EDGE,"E471.bottom");var subQ10=makeQuery(id+"F5.opExtrude","CAP_FACE",FACE,{"disambiguationData":[OSD([subQ9,subQ8,subQ7,subQ6,subQ5,subQ4,subQ3,subQ2])],"isStart":false});Q3=makeQuery(id+"F15.boolean.opBoolean","SPLIT",EDGE,{"disambiguationData":[TD([makeQuery(id+"F7.opFillet","BLEND_FACE",FACE,{"disambiguationData":[OSD([subQ0,subQ9,subQ8,subQ7,subQ6,subQ5,subQ4,subQ3,subQ2])]})])],"derivedFrom":makeQuery(id+"F6.opBoolean","INTERSECT",EDGE,{"derivedFrom":[subQ1,subQ10]})});}
            fillet(context, id + "F19", {"entities" : qUnion([Q0, Q1, Q2, Q3]), "radius" : 2 * mm, "tangentPropagation" : true, "allowEdgeOverflow" : false});
        }
        {
            var Q0;
            Q0=qCreatedBy(makeId("Right.planeOp"),FACE);
            var sketch = newSketch(context, id + "F20", { "sketchPlane" : qUnion([Q0])});
            skLineSegment(sketch, "E496", {"start": v(0, 0) * mm, "end": v(-7, 0) * mm, "construction": true});
            skLineSegment(sketch, "E497", {"start": v(0, 0) * mm, "end": v(7, 0) * mm, "construction": true});
            skArc(sketch, "E498", {"start": v(7, 0) * mm, "mid": v(0, 2.51) * mm, "end": v(-7, 0) * mm});
            skLineSegment(sketch, "E499", {"start": v(-7, 0) * mm, "end": v(-7, 4.65) * mm});
            skLineSegment(sketch, "E500", {"start": v(-7, 4.65) * mm, "end": v(7, 4.65) * mm});
            skLineSegment(sketch, "E501", {"start": v(7, 4.65) * mm, "end": v(7, 0) * mm});
            skSolve(sketch);
        }
        {
            var Q0;
            Q0 = qSketchRegion(id + "F20", true);
            extrude(context, id + "F21", {"entities" : qUnion([Q0]), "operationType" : NewBodyOperationType.REMOVE, "depth" : 38.1 * mm, "offsetDistance" : 25 * mm, "hasSecondDirection" : true, "secondDirectionOppositeDirection" : true, "secondDirectionDepth" : 25 * mm});
        }
    });
